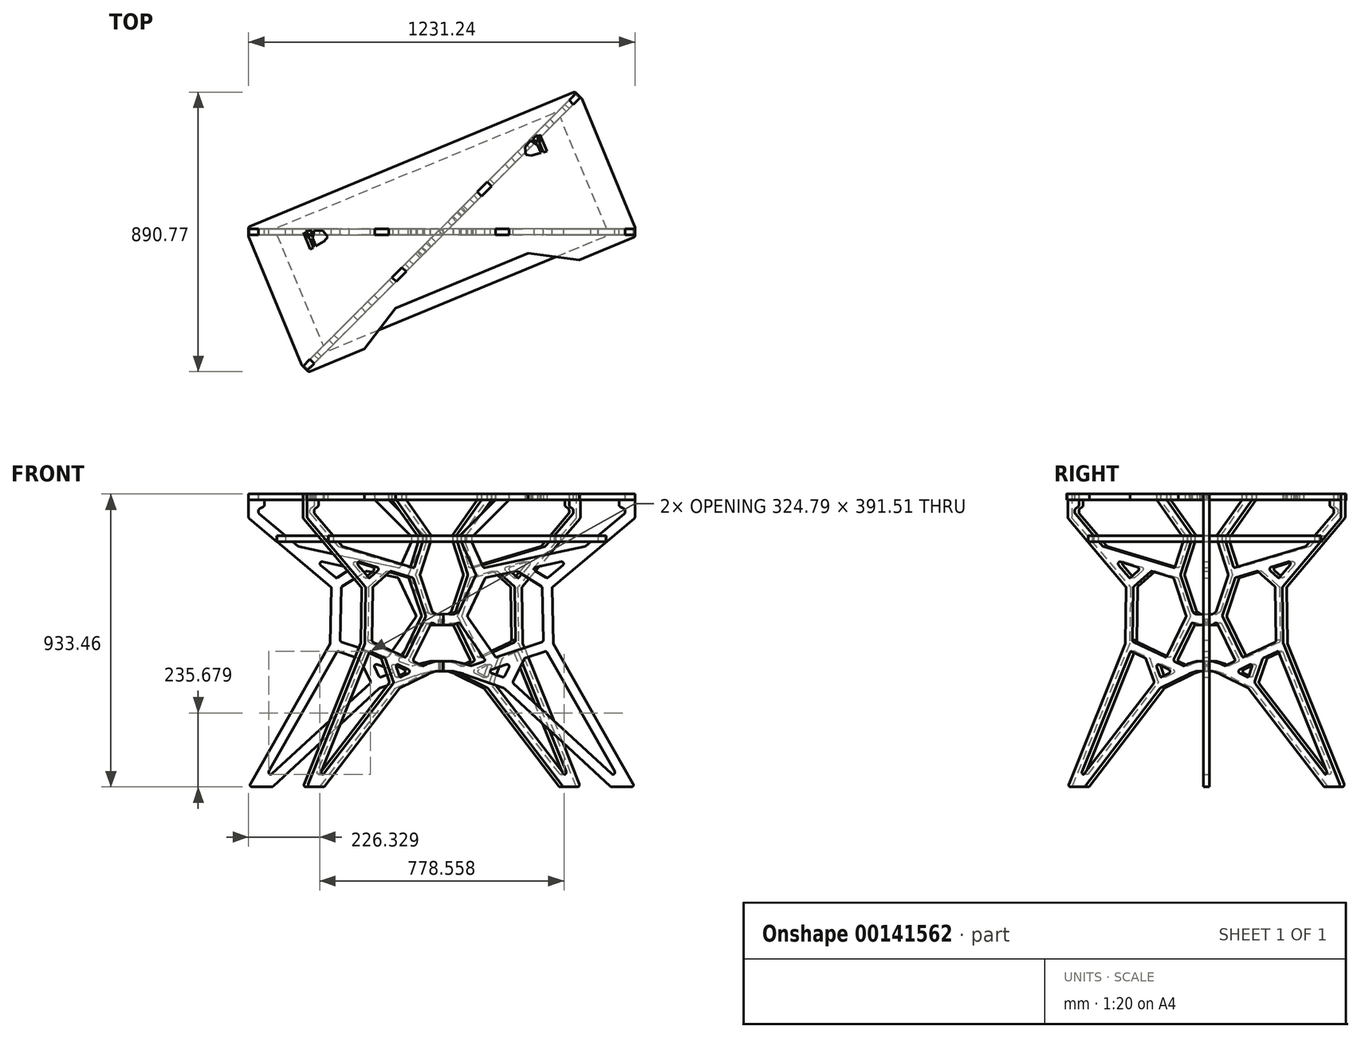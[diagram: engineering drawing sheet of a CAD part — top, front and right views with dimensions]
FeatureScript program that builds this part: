
annotation { "Feature Type Name" : "Feature", "Feature Type Description" : "" }
export const myFeature = defineFeature(function(context is Context, id is Id, definition is map)
    precondition{}
    {
        {
            var Q0;
            Q0=qCreatedBy(makeId("Front.planeOp"),FACE);
            var sketch = newSketch(context, id + "F0", { "sketchPlane" : qUnion([Q0])});
            skLineSegment(sketch, "E0.bottom", {"start": v(-726.46, -550.82) * mm, "end": v(-663.66, -550.82) * mm});
            skLineSegment(sketch, "E0.top", {"start": v(-737.38, 382.63) * mm, "end": v(-705.63, 382.63) * mm});
            skLineSegment(sketch, "E0.left", {"start": v(-737.38, -93.62) * mm, "end": v(-737.38, 230.23) * mm});
            skLineSegment(sketch, "E1", {"start": v(-705.63, 363.58) * mm, "end": v(-686.58, 363.58) * mm});
            skLineSegment(sketch, "E2.bottom", {"start": v(-737.38, 230.23) * mm, "end": v(493.44, 230.23) * mm, "construction": true});
            skLineSegment(sketch, "E2.top", {"start": v(-737.38, 211.18) * mm, "end": v(493.44, 211.18) * mm, "construction": true});
            skLineSegment(sketch, "E2.left", {"start": v(-737.38, 230.23) * mm, "end": v(-737.38, 211.18) * mm});
            skLineSegment(sketch, "E2.right", {"start": v(493.44, 230.23) * mm, "end": v(493.44, 211.18) * mm});
            skLineSegment(sketch, "E3", {"start": v(-735.1, 304.53) * mm, "end": v(-475.84, 87.44) * mm});
            skLineSegment(sketch, "E4", {"start": v(-473.57, 82.44) * mm, "end": v(-477.15, -92) * mm});
            skLineSegment(sketch, "E5", {"start": v(-477.98, -95.02) * mm, "end": v(-731.98, -541.32) * mm});
            skLineSegment(sketch, "E6", {"start": v(-737.38, -93.62) * mm, "end": v(493.78, -93.62) * mm, "construction": true});
            skLineSegment(sketch, "E7", {"start": v(-726.46, -550.82) * mm, "end": v(-661.18, -550.82) * mm});
            skLineSegment(sketch, "E8", {"start": v(-659.36, -549.13) * mm, "end": v(-321.3, -237.33) * mm});
            skLineSegment(sketch, "E9", {"start": v(-319.11, -236) * mm, "end": v(-190.82, -190.7) * mm});
            skLineSegment(sketch, "E10", {"start": v(-190.2, -190.52) * mm, "end": v(-123.3, -174.31) * mm});
            skLineSegment(sketch, "E11", {"start": v(-182.24, 230.23) * mm, "end": v(-228.58, 128.01) * mm});
            skLineSegment(sketch, "E12", {"start": v(-228.55, 122.7) * mm, "end": v(-175.03, 8.55) * mm});
            skLineSegment(sketch, "E13", {"start": v(-171.72, 5.38) * mm, "end": v(-124.24, -14.36) * mm});
            skLineSegment(sketch, "E14", {"start": v(-553, 193.46) * mm, "end": v(-261.6, 132.05) * mm, "construction": true});
            skLineSegment(sketch, "E15", {"start": v(-473.5, 85.48) * mm, "end": v(-383.92, 141.6) * mm, "construction": true});
            skLineSegment(sketch, "E16", {"start": v(-477.18, -93.62) * mm, "end": v(-239.21, -174.12) * mm, "construction": true});
            skLineSegment(sketch, "E17", {"start": v(-320.34, -236.44) * mm, "end": v(-364, -148.67) * mm, "construction": true});
            skLineSegment(sketch, "E18", {"start": v(-192.54, -20.35) * mm, "end": v(-278.62, -144.03) * mm, "construction": true});
            skLineSegment(sketch, "E19.0", {"start": v(-662.9, -509.21) * mm, "end": v(-350.73, -221.27) * mm});
            skLineSegment(sketch, "E20.0", {"start": v(-457.14, -122.59) * mm, "end": v(-672.73, -501.4) * mm});
            skLineSegment(sketch, "E21.0", {"start": v(-199.25, -160.05) * mm, "end": v(-123.3, -141.64) * mm});
            skLineSegment(sketch, "E21.1", {"start": v(-314.2, -200.6) * mm, "end": v(-280.77, -188.8) * mm});
            skLineSegment(sketch, "E22.0", {"start": v(-172.82, -28.55) * mm, "end": v(-124.24, -48.75) * mm});
            skLineSegment(sketch, "E22.1", {"start": v(-258.92, 112.68) * mm, "end": v(-204.28, -3.86) * mm});
            skLineSegment(sketch, "E23.0", {"start": v(-705.63, 324.22) * mm, "end": v(-705.63, 329.87) * mm});
            skLineSegment(sketch, "E24.0", {"start": v(-703.36, 319.36) * mm, "end": v(-580.12, 216.16) * mm});
            skLineSegment(sketch, "E25.0", {"start": v(-441.8, 83.23) * mm, "end": v(-445.22, -83.58) * mm});
            skLineSegment(sketch, "E26.0", {"start": v(-502.23, 166.54) * mm, "end": v(-421.69, 149.57) * mm});
            skLineSegment(sketch, "E27.0", {"start": v(-577.35, 214.82) * mm, "end": v(-259.88, 147.91) * mm});
            skLineSegment(sketch, "E28.0", {"start": v(-438.82, 88.48) * mm, "end": v(-363.71, 135.53) * mm});
            skLineSegment(sketch, "E29.0", {"start": v(-454.1, 116.37) * mm, "end": v(-419.62, 137.97) * mm});
            skLineSegment(sketch, "E30.0", {"start": v(-440.92, -89.12) * mm, "end": v(-298.8, -137.2) * mm});
            skLineSegment(sketch, "E31.0", {"start": v(-449.58, -119.71) * mm, "end": v(-387.8, -140.61) * mm});
            skLineSegment(sketch, "E32.0", {"start": v(-322, -197.44) * mm, "end": v(-335.83, -169.65) * mm});
            skLineSegment(sketch, "E33.0", {"start": v(-349.34, -213.78) * mm, "end": v(-384.15, -143.8) * mm});
            skLineSegment(sketch, "E34.0", {"start": v(-204.81, -10.18) * mm, "end": v(-291.55, -134.82) * mm});
            skLineSegment(sketch, "E35.0", {"start": v(-180.47, -30.78) * mm, "end": v(-258.14, -142.4) * mm});
            skLineSegment(sketch, "E36.trimOffspring", {"start": v(-507.62, 155.46) * mm, "end": v(-461.55, 116.88) * mm});
            skLineSegment(sketch, "E37.trimOffspring", {"start": v(-359.03, 136.36) * mm, "end": v(-263.36, 116.2) * mm});
            skLineSegment(sketch, "E38.trimOffspring", {"start": v(-254.96, -152.04) * mm, "end": v(-217.05, -164.86) * mm});
            skLineSegment(sketch, "E39.trimOffspring", {"start": v(-328.1, -160.8) * mm, "end": v(-280.85, -176.8) * mm});
            skLineSegment(sketch, "E40", {"start": v(-217.45, 230.23) * mm, "end": v(-182.24, 230.23) * mm});
            skPoint(sketch, "E41.orphan", {"position": v(-121.8, 363.58) * mm});
            skLineSegment(sketch, "E42.trimOffspring", {"start": v(-217.45, 230.23) * mm, "end": v(-252.78, 151.53) * mm});
            skPoint(sketch, "E43.visualSharp", {"position": v(-319.5, -202.47) * mm});
            skArc(sketch, "E43.filletArc", {"start": v(-322, -197.44) * mm, "mid": v(-318.7, -200.5) * mm, "end": v(-314.2, -200.6) * mm});
            skLineSegment(sketch, "E44.trimOffspring", {"start": v(-212.9, -164.83) * mm, "end": v(-199.87, -160.23) * mm});
            skPoint(sketch, "E45.visualSharp", {"position": v(-342.68, -155.88) * mm});
            skArc(sketch, "E45.filletArc", {"start": v(-328.1, -160.8) * mm, "mid": v(-334.93, -162.65) * mm, "end": v(-335.83, -169.65) * mm});
            skPoint(sketch, "E46.visualSharp", {"position": v(-263.45, -182.68) * mm});
            skArc(sketch, "E46.filletArc", {"start": v(-280.77, -188.8) * mm, "mid": v(-276.54, -182.77) * mm, "end": v(-280.85, -176.8) * mm});
            skPoint(sketch, "E47.visualSharp", {"position": v(-347.22, -218.04) * mm});
            skArc(sketch, "E47.filletArc", {"start": v(-350.73, -221.27) * mm, "mid": v(-348.79, -217.75) * mm, "end": v(-349.34, -213.78) * mm});
            skPoint(sketch, "E48.visualSharp", {"position": v(-385.31, -141.45) * mm});
            skArc(sketch, "E48.filletArc", {"start": v(-384.15, -143.8) * mm, "mid": v(-385.65, -141.85) * mm, "end": v(-387.8, -140.61) * mm});
            skPoint(sketch, "E49.visualSharp", {"position": v(-454.54, -118.03) * mm});
            skArc(sketch, "E49.filletArc", {"start": v(-449.58, -119.71) * mm, "mid": v(-453.88, -119.8) * mm, "end": v(-457.14, -122.59) * mm});
            skPoint(sketch, "E50.visualSharp", {"position": v(-692.94, -536.91) * mm});
            skArc(sketch, "E50.filletArc", {"start": v(-672.73, -501.4) * mm, "mid": v(-671.16, -509.51) * mm, "end": v(-662.9, -509.21) * mm});
            skPoint(sketch, "E51.visualSharp", {"position": v(-445.33, -87.63) * mm});
            skArc(sketch, "E51.filletArc", {"start": v(-445.23, -82.98) * mm, "mid": v(-444.08, -86.76) * mm, "end": v(-440.92, -89.12) * mm});
            skPoint(sketch, "E52.visualSharp", {"position": v(-294.28, -138.74) * mm});
            skArc(sketch, "E52.filletArc", {"start": v(-298.8, -137.2) * mm, "mid": v(-294.78, -137.22) * mm, "end": v(-291.55, -134.82) * mm});
            skPoint(sketch, "E53.visualSharp", {"position": v(-262.97, -149.33) * mm});
            skArc(sketch, "E53.filletArc", {"start": v(-258.14, -142.4) * mm, "mid": v(-258.96, -148) * mm, "end": v(-254.96, -152.04) * mm});
            skPoint(sketch, "E54.visualSharp", {"position": v(-214.97, -165.57) * mm});
            skArc(sketch, "E54.filletArc", {"start": v(-217.05, -164.86) * mm, "mid": v(-214.98, -165.2) * mm, "end": v(-212.9, -164.83) * mm});
            skPoint(sketch, "E55.visualSharp", {"position": v(-199.56, -160.12) * mm});
            skArc(sketch, "E55.filletArc", {"start": v(-199.25, -160.05) * mm, "mid": v(-199.56, -160.13) * mm, "end": v(-199.87, -160.23) * mm});
            skPoint(sketch, "E56.visualSharp", {"position": v(-190.51, -190.6) * mm});
            skArc(sketch, "E56.filletArc", {"start": v(-190.2, -190.52) * mm, "mid": v(-190.51, -190.6) * mm, "end": v(-190.82, -190.7) * mm});
            skPoint(sketch, "E57.visualSharp", {"position": v(-320.34, -236.44) * mm});
            skArc(sketch, "E57.filletArc", {"start": v(-319.11, -236) * mm, "mid": v(-320.27, -236.55) * mm, "end": v(-321.3, -237.33) * mm});
            skPoint(sketch, "E58.visualSharp", {"position": v(-177.54, -26.58) * mm});
            skArc(sketch, "E58.filletArc", {"start": v(-172.82, -28.55) * mm, "mid": v(-177.04, -28.32) * mm, "end": v(-180.47, -30.78) * mm});
            skPoint(sketch, "E59.visualSharp", {"position": v(-173.99, 6.32) * mm});
            skArc(sketch, "E59.filletArc", {"start": v(-175.03, 8.55) * mm, "mid": v(-173.67, 6.65) * mm, "end": v(-171.72, 5.38) * mm});
            skPoint(sketch, "E60.visualSharp", {"position": v(-202.72, -7.18) * mm});
            skArc(sketch, "E60.filletArc", {"start": v(-204.81, -10.18) * mm, "mid": v(-203.7, -7.1) * mm, "end": v(-204.28, -3.86) * mm});
            skPoint(sketch, "E61.visualSharp", {"position": v(-477.18, -93.62) * mm});
            skArc(sketch, "E61.filletArc", {"start": v(-477.98, -95.02) * mm, "mid": v(-477.37, -93.56) * mm, "end": v(-477.15, -92) * mm});
            skPoint(sketch, "E62.visualSharp", {"position": v(-473.5, 85.48) * mm});
            skArc(sketch, "E62.filletArc", {"start": v(-473.57, 82.44) * mm, "mid": v(-474.14, 85.2) * mm, "end": v(-475.84, 87.44) * mm});
            skPoint(sketch, "E63.visualSharp", {"position": v(-441.73, 86.66) * mm});
            skArc(sketch, "E63.filletArc", {"start": v(-438.82, 88.48) * mm, "mid": v(-440.97, 86.23) * mm, "end": v(-441.8, 83.23) * mm});
            skPoint(sketch, "E64.visualSharp", {"position": v(-458.02, 113.92) * mm});
            skArc(sketch, "E64.filletArc", {"start": v(-461.55, 116.88) * mm, "mid": v(-457.91, 115.42) * mm, "end": v(-454.1, 116.37) * mm});
            skPoint(sketch, "E65.visualSharp", {"position": v(-260.26, 115.55) * mm});
            skArc(sketch, "E65.filletArc", {"start": v(-258.92, 112.68) * mm, "mid": v(-260.72, 114.96) * mm, "end": v(-263.36, 116.2) * mm});
            skPoint(sketch, "E66.visualSharp", {"position": v(-361.54, 136.89) * mm});
            skArc(sketch, "E66.filletArc", {"start": v(-359.03, 136.36) * mm, "mid": v(-361.45, 136.4) * mm, "end": v(-363.71, 135.53) * mm});
            skPoint(sketch, "E67.visualSharp", {"position": v(-406.3, 146.32) * mm});
            skArc(sketch, "E67.filletArc", {"start": v(-419.62, 137.97) * mm, "mid": v(-416.74, 144.46) * mm, "end": v(-421.69, 149.57) * mm});
            skPoint(sketch, "E68.visualSharp", {"position": v(-254.88, 146.86) * mm});
            skArc(sketch, "E68.filletArc", {"start": v(-259.88, 147.91) * mm, "mid": v(-255.7, 148.47) * mm, "end": v(-252.78, 151.53) * mm});
            skPoint(sketch, "E69.visualSharp", {"position": v(-229.79, 125.35) * mm});
            skArc(sketch, "E69.filletArc", {"start": v(-228.58, 128.01) * mm, "mid": v(-229.15, 125.35) * mm, "end": v(-228.55, 122.7) * mm});
            skPoint(sketch, "E70.visualSharp", {"position": v(-527.12, 171.78) * mm});
            skArc(sketch, "E70.filletArc", {"start": v(-502.23, 166.54) * mm, "mid": v(-509.25, 163.1) * mm, "end": v(-507.62, 155.46) * mm});
            skPoint(sketch, "E71.visualSharp", {"position": v(-578.9, 215.14) * mm});
            skArc(sketch, "E71.filletArc", {"start": v(-580.12, 216.16) * mm, "mid": v(-578.82, 215.32) * mm, "end": v(-577.35, 214.82) * mm});
            skLineSegment(sketch, "E72", {"start": v(-737.38, 382.63) * mm, "end": v(-737.38, 309.4) * mm});
            skPoint(sketch, "E73.visualSharp", {"position": v(-737.38, 306.43) * mm});
            skArc(sketch, "E73.filletArc", {"start": v(-737.38, 309.4) * mm, "mid": v(-736.78, 306.71) * mm, "end": v(-735.1, 304.53) * mm});
            skPoint(sketch, "E74.visualSharp", {"position": v(-705.63, 321.26) * mm});
            skArc(sketch, "E74.filletArc", {"start": v(-705.63, 324.22) * mm, "mid": v(-705.03, 321.54) * mm, "end": v(-703.36, 319.36) * mm});
            skArc(sketch, "E75.MirrorCS", {"start": v(234.38, -95.02) * mm, "mid": v(233.78, -93.56) * mm, "end": v(233.55, -92) * mm});
            skArc(sketch, "E76.MirrorCS", {"start": v(195.22, 88.48) * mm, "mid": v(197.38, 86.23) * mm, "end": v(198.2, 83.23) * mm});
            skArc(sketch, "E77.MirrorCS", {"start": v(-26.54, -164.86) * mm, "mid": v(-28.62, -165.2) * mm, "end": v(-30.7, -164.83) * mm});
            skArc(sketch, "E78.MirrorCS", {"start": v(-44.35, -160.05) * mm, "mid": v(-44.04, -160.13) * mm, "end": v(-43.73, -160.23) * mm});
            skLineSegment(sketch, "E79.MirrorCS", {"start": v(-30.7, -164.83) * mm, "end": v(-43.73, -160.23) * mm});
            skArc(sketch, "E80.MirrorCS", {"start": v(229.97, 82.44) * mm, "mid": v(230.54, 85.2) * mm, "end": v(232.25, 87.44) * mm});
            skArc(sketch, "E81.MirrorCS", {"start": v(75.51, -236) * mm, "mid": v(76.68, -236.55) * mm, "end": v(77.7, -237.33) * mm});
            skLineSegment(sketch, "E82.MirrorCS", {"start": v(78.41, -197.44) * mm, "end": v(92.23, -169.65) * mm});
            skArc(sketch, "E83.MirrorCS", {"start": v(-70.78, -28.55) * mm, "mid": v(-66.56, -28.32) * mm, "end": v(-63.13, -30.78) * mm});
            skArc(sketch, "E84.MirrorCS", {"start": v(-53.4, -190.52) * mm, "mid": v(-53.08, -190.6) * mm, "end": v(-52.78, -190.7) * mm});
            skArc(sketch, "E85.MirrorCS", {"start": v(115.43, 136.36) * mm, "mid": v(117.86, 136.4) * mm, "end": v(120.11, 135.53) * mm});
            skArc(sketch, "E86.MirrorCS", {"start": v(78.41, -197.44) * mm, "mid": v(75.1, -200.5) * mm, "end": v(70.61, -200.6) * mm});
            skArc(sketch, "E87.MirrorCS", {"start": v(84.51, -160.8) * mm, "mid": v(91.33, -162.65) * mm, "end": v(92.23, -169.65) * mm});
            skArc(sketch, "E88.MirrorCS", {"start": v(336.52, 216.16) * mm, "mid": v(335.22, 215.32) * mm, "end": v(333.75, 214.82) * mm});
            skArc(sketch, "E89.MirrorCS", {"start": v(15.32, 112.68) * mm, "mid": v(17.13, 114.96) * mm, "end": v(19.76, 116.2) * mm});
            skArc(sketch, "E90.MirrorCS", {"start": v(462.03, 324.22) * mm, "mid": v(461.44, 321.54) * mm, "end": v(459.76, 319.36) * mm});
            skArc(sketch, "E91.MirrorCS", {"start": v(217.96, 116.88) * mm, "mid": v(214.32, 115.42) * mm, "end": v(210.5, 116.37) * mm});
            skArc(sketch, "E92.MirrorCS", {"start": v(140.55, -143.8) * mm, "mid": v(142.06, -141.85) * mm, "end": v(144.2, -140.61) * mm});
            skArc(sketch, "E93.MirrorCS", {"start": v(16.29, 147.91) * mm, "mid": v(12.1, 148.47) * mm, "end": v(9.19, 151.53) * mm});
            skArc(sketch, "E94.MirrorCS", {"start": v(-68.57, 8.55) * mm, "mid": v(-69.93, 6.65) * mm, "end": v(-71.88, 5.38) * mm});
            skArc(sketch, "E95.MirrorCS", {"start": v(107.13, -221.27) * mm, "mid": v(105.19, -217.75) * mm, "end": v(105.75, -213.78) * mm});
            skArc(sketch, "E96.MirrorCS", {"start": v(55.2, -137.2) * mm, "mid": v(51.18, -137.22) * mm, "end": v(47.95, -134.82) * mm});
            skLineSegment(sketch, "E97.MirrorCS", {"start": v(210.5, 116.37) * mm, "end": v(176.03, 137.97) * mm});
            skLineSegment(sketch, "E98.MirrorCS", {"start": v(76.75, -236.44) * mm, "end": v(120.4, -148.67) * mm, "construction": true});
            skArc(sketch, "E99.MirrorCS", {"start": v(-15.02, 128.01) * mm, "mid": v(-14.45, 125.35) * mm, "end": v(-15.05, 122.7) * mm});
            skArc(sketch, "E100.MirrorCS", {"start": v(176.03, 137.97) * mm, "mid": v(173.15, 144.46) * mm, "end": v(178.09, 149.57) * mm});
            skArc(sketch, "E101.MirrorCS", {"start": v(201.64, -82.98) * mm, "mid": v(200.49, -86.76) * mm, "end": v(197.32, -89.12) * mm});
            skArc(sketch, "E102.MirrorCS", {"start": v(205.99, -119.71) * mm, "mid": v(210.28, -119.8) * mm, "end": v(213.54, -122.59) * mm});
            skArc(sketch, "E103.MirrorCS", {"start": v(493.78, 309.4) * mm, "mid": v(493.19, 306.71) * mm, "end": v(491.5, 304.53) * mm});
            skArc(sketch, "E104.MirrorCS", {"start": v(258.64, 166.54) * mm, "mid": v(265.66, 163.1) * mm, "end": v(264.02, 155.46) * mm});
            skLineSegment(sketch, "E105.MirrorCS", {"start": v(11.37, -152.04) * mm, "end": v(-26.54, -164.86) * mm});
            skLineSegment(sketch, "E106.MirrorCS", {"start": v(493.78, -550.82) * mm, "end": v(417.58, -550.82) * mm});
            skLineSegment(sketch, "E107.MirrorCS", {"start": v(70.61, -200.6) * mm, "end": v(37.18, -188.8) * mm});
            skLineSegment(sketch, "E108.MirrorCS", {"start": v(493.78, 230.23) * mm, "end": v(493.78, 211.18) * mm});
            skArc(sketch, "E109.MirrorCS", {"start": v(429.13, -501.4) * mm, "mid": v(427.56, -509.51) * mm, "end": v(419.3, -509.21) * mm});
            skLineSegment(sketch, "E110.MirrorCS", {"start": v(84.51, -160.8) * mm, "end": v(37.26, -176.8) * mm});
            skArc(sketch, "E111.MirrorCS", {"start": v(37.18, -188.8) * mm, "mid": v(32.94, -182.77) * mm, "end": v(37.26, -176.8) * mm});
            skArc(sketch, "E112.MirrorCS", {"start": v(14.54, -142.4) * mm, "mid": v(15.36, -148) * mm, "end": v(11.37, -152.04) * mm});
            skArc(sketch, "E113.MirrorCS", {"start": v(-38.78, -10.18) * mm, "mid": v(-39.9, -7.1) * mm, "end": v(-39.32, -3.86) * mm});
            skLineSegment(sketch, "E114.MirrorCS", {"start": v(229.91, 85.48) * mm, "end": v(140.32, 141.6) * mm, "construction": true});
            skLineSegment(sketch, "E115.MirrorCS", {"start": v(105.75, -213.78) * mm, "end": v(140.55, -143.8) * mm});
            skLineSegment(sketch, "E116.MirrorCS", {"start": v(-26.15, 230.23) * mm, "end": v(-61.35, 230.23) * mm});
            skLineSegment(sketch, "E117.MirrorCS", {"start": v(264.02, 155.46) * mm, "end": v(217.96, 116.88) * mm});
            skLineSegment(sketch, "E118.MirrorCS", {"start": v(462.03, 324.22) * mm, "end": v(462.03, 329.87) * mm});
            skLineSegment(sketch, "E119.MirrorCS", {"start": v(-737.04, 230.23) * mm, "end": v(-737.04, 211.18) * mm});
            skLineSegment(sketch, "E120.MirrorCS", {"start": v(482.86, -550.82) * mm, "end": v(420.06, -550.82) * mm});
            skLineSegment(sketch, "E121.MirrorCS", {"start": v(-71.88, 5.38) * mm, "end": v(-119.36, -14.36) * mm});
            skPoint(sketch, "E122.MirrorP", {"position": v(-28.62, -165.57) * mm});
            skLineSegment(sketch, "E123.MirrorCS", {"start": v(-38.78, -10.18) * mm, "end": v(47.95, -134.82) * mm});
            skLineSegment(sketch, "E124.MirrorCS", {"start": v(-51.05, -20.35) * mm, "end": v(35.03, -144.03) * mm, "construction": true});
            skLineSegment(sketch, "E125.MirrorCS", {"start": v(309.41, 193.46) * mm, "end": v(18.01, 132.05) * mm, "construction": true});
            skLineSegment(sketch, "E126.MirrorCS", {"start": v(233.58, -93.62) * mm, "end": v(-4.38, -174.12) * mm, "construction": true});
            skLineSegment(sketch, "E127.MirrorCS", {"start": v(258.64, 166.54) * mm, "end": v(178.09, 149.57) * mm});
            skPoint(sketch, "E128.MirrorP", {"position": v(99.08, -155.88) * mm});
            skLineSegment(sketch, "E129.MirrorCS", {"start": v(-70.78, -28.55) * mm, "end": v(-119.36, -48.75) * mm});
            skPoint(sketch, "E130.MirrorP", {"position": v(-66.05, -26.58) * mm});
            skPoint(sketch, "E131.MirrorP", {"position": v(162.7, 146.32) * mm});
            skPoint(sketch, "E132.MirrorP", {"position": v(198.13, 86.66) * mm});
            skLineSegment(sketch, "E133.MirrorCS", {"start": v(-63.13, -30.78) * mm, "end": v(14.54, -142.4) * mm});
            skLineSegment(sketch, "E134.MirrorCS", {"start": v(205.99, -119.71) * mm, "end": v(144.2, -140.61) * mm});
            skLineSegment(sketch, "E135.MirrorCS", {"start": v(195.22, 88.48) * mm, "end": v(120.11, 135.53) * mm});
            skPoint(sketch, "E136.MirrorP", {"position": v(50.68, -138.74) * mm});
            skLineSegment(sketch, "E137.MirrorCS", {"start": v(-44.35, -160.05) * mm, "end": v(-120.3, -141.64) * mm});
            skLineSegment(sketch, "E138.MirrorCS", {"start": v(-53.4, -190.52) * mm, "end": v(-120.3, -174.31) * mm});
            skLineSegment(sketch, "E139.MirrorCS", {"start": v(197.32, -89.12) * mm, "end": v(55.2, -137.2) * mm});
            skPoint(sketch, "E140.MirrorP", {"position": v(462.03, 321.26) * mm});
            skPoint(sketch, "E141.MirrorP", {"position": v(16.66, 115.55) * mm});
            skPoint(sketch, "E142.MirrorP", {"position": v(-40.87, -7.18) * mm});
            skPoint(sketch, "E143.MirrorP", {"position": v(11.28, 146.86) * mm});
            skLineSegment(sketch, "E144.MirrorCS", {"start": v(-26.15, 230.23) * mm, "end": v(9.19, 151.53) * mm});
            skLineSegment(sketch, "E145.MirrorCS", {"start": v(419.3, -509.21) * mm, "end": v(107.13, -221.27) * mm});
            skLineSegment(sketch, "E146.MirrorCS", {"start": v(-15.05, 122.7) * mm, "end": v(-68.57, 8.55) * mm});
            skLineSegment(sketch, "E147.MirrorCS", {"start": v(198.2, 83.23) * mm, "end": v(201.62, -83.58) * mm});
            skLineSegment(sketch, "E148.MirrorCS", {"start": v(459.76, 319.36) * mm, "end": v(336.52, 216.16) * mm});
            skLineSegment(sketch, "E149.MirrorCS", {"start": v(493.78, 382.63) * mm, "end": v(493.78, 309.4) * mm});
            skPoint(sketch, "E150.MirrorP", {"position": v(19.86, -182.68) * mm});
            skPoint(sketch, "E151.MirrorP", {"position": v(214.42, 113.92) * mm});
            skLineSegment(sketch, "E152.MirrorCS", {"start": v(-61.35, 230.23) * mm, "end": v(-15.02, 128.01) * mm});
            skPoint(sketch, "E153.MirrorP", {"position": v(283.52, 171.78) * mm});
            skPoint(sketch, "E154.MirrorP", {"position": v(141.72, -141.45) * mm});
            skPoint(sketch, "E155.MirrorP", {"position": v(493.78, 306.43) * mm});
            skPoint(sketch, "E156.MirrorP", {"position": v(229.91, 85.48) * mm});
            skLineSegment(sketch, "E157.MirrorCS", {"start": v(213.54, -122.59) * mm, "end": v(429.13, -501.4) * mm});
            skLineSegment(sketch, "E158.MirrorCS", {"start": v(493.78, -93.62) * mm, "end": v(493.78, 230.23) * mm});
            skPoint(sketch, "E159.MirrorP", {"position": v(19.37, -149.33) * mm});
            skLineSegment(sketch, "E160.MirrorCS", {"start": v(333.75, 214.82) * mm, "end": v(16.29, 147.91) * mm});
            skPoint(sketch, "E161.MirrorP", {"position": v(335.3, 215.14) * mm});
            skLineSegment(sketch, "E162.MirrorCS", {"start": v(491.5, 304.53) * mm, "end": v(232.25, 87.44) * mm});
            skPoint(sketch, "E163.MirrorP", {"position": v(75.9, -202.47) * mm});
            skPoint(sketch, "E164.MirrorP", {"position": v(-53.08, -190.6) * mm});
            skLineSegment(sketch, "E165.MirrorCS", {"start": v(75.51, -236) * mm, "end": v(-52.78, -190.7) * mm});
            skPoint(sketch, "E166.MirrorP", {"position": v(117.94, 136.89) * mm});
            skPoint(sketch, "E167.MirrorP", {"position": v(-13.8, 125.35) * mm});
            skLineSegment(sketch, "E168.MirrorCS", {"start": v(415.76, -549.13) * mm, "end": v(77.7, -237.33) * mm});
            skLineSegment(sketch, "E169.MirrorCS", {"start": v(234.38, -95.02) * mm, "end": v(488.38, -541.32) * mm});
            skPoint(sketch, "E170.MirrorP", {"position": v(210.95, -118.03) * mm});
            skLineSegment(sketch, "E171.MirrorCS", {"start": v(15.32, 112.68) * mm, "end": v(-39.32, -3.86) * mm});
            skPoint(sketch, "E172.MirrorP", {"position": v(-69.61, 6.32) * mm});
            skPoint(sketch, "E173.MirrorP", {"position": v(-44.04, -160.12) * mm});
            skPoint(sketch, "E174.MirrorP", {"position": v(76.75, -236.44) * mm});
            skPoint(sketch, "E175.MirrorP", {"position": v(103.63, -218.04) * mm});
            skPoint(sketch, "E176.MirrorP", {"position": v(201.73, -87.63) * mm});
            skLineSegment(sketch, "E177.MirrorCS", {"start": v(229.97, 82.44) * mm, "end": v(233.55, -92) * mm});
            skLineSegment(sketch, "E178.MirrorCS", {"start": v(115.43, 136.36) * mm, "end": v(19.76, 116.2) * mm});
            skPoint(sketch, "E179.MirrorP", {"position": v(233.58, -93.62) * mm});
            skLineSegment(sketch, "E180", {"start": v(-686.58, 363.58) * mm, "end": v(-686.58, 348.2) * mm});
            skLineSegment(sketch, "E181", {"start": v(-689.75, 342.7) * mm, "end": v(-702.45, 335.37) * mm});
            skLineSegment(sketch, "E182.trimOffspring", {"start": v(-705.63, 363.58) * mm, "end": v(-705.63, 382.63) * mm});
            skPoint(sketch, "E183.visualSharp", {"position": v(-705.63, 333.54) * mm});
            skArc(sketch, "E183.filletArc", {"start": v(-702.45, 335.37) * mm, "mid": v(-704.78, 333.04) * mm, "end": v(-705.63, 329.87) * mm});
            skPoint(sketch, "E184.visualSharp", {"position": v(-686.58, 344.53) * mm});
            skArc(sketch, "E184.filletArc", {"start": v(-689.75, 342.7) * mm, "mid": v(-687.43, 345.03) * mm, "end": v(-686.58, 348.2) * mm});
            skLineSegment(sketch, "E185.trimOffspring", {"start": v(462.03, 382.63) * mm, "end": v(493.78, 382.63) * mm});
            skLineSegment(sketch, "E186", {"start": v(-182.24, 230.23) * mm, "end": v(-182.24, 249.28) * mm});
            skLineSegment(sketch, "E187", {"start": v(-182.24, 249.28) * mm, "end": v(-217.45, 249.28) * mm});
            skLineSegment(sketch, "E188", {"start": v(-217.45, 249.28) * mm, "end": v(-217.45, 230.23) * mm});
            skLineSegment(sketch, "E189", {"start": v(-61.35, 230.23) * mm, "end": v(-61.35, 249.28) * mm});
            skLineSegment(sketch, "E190", {"start": v(-61.35, 249.28) * mm, "end": v(-26.15, 249.28) * mm});
            skLineSegment(sketch, "E191", {"start": v(-26.15, 249.28) * mm, "end": v(-26.15, 230.23) * mm});
            skLineSegment(sketch, "E192", {"start": v(462.03, 363.58) * mm, "end": v(442.98, 363.58) * mm});
            skLineSegment(sketch, "E193", {"start": v(442.98, 363.58) * mm, "end": v(442.98, 348.2) * mm});
            skLineSegment(sketch, "E194", {"start": v(446.16, 342.7) * mm, "end": v(458.86, 335.37) * mm});
            skLineSegment(sketch, "E195.trimOffspring", {"start": v(462.03, 363.58) * mm, "end": v(462.03, 382.63) * mm});
            skPoint(sketch, "E196.visualSharp", {"position": v(442.98, 344.53) * mm});
            skArc(sketch, "E196.filletArc", {"start": v(442.98, 348.2) * mm, "mid": v(443.83, 345.03) * mm, "end": v(446.16, 342.7) * mm});
            skPoint(sketch, "E197.visualSharp", {"position": v(462.03, 333.54) * mm});
            skArc(sketch, "E197.filletArc", {"start": v(462.03, 329.87) * mm, "mid": v(461.18, 333.04) * mm, "end": v(458.86, 335.37) * mm});
            skPoint(sketch, "E198.visualSharp", {"position": v(417.58, -550.82) * mm});
            skArc(sketch, "E198.filletArc", {"start": v(415.76, -549.13) * mm, "mid": v(417.75, -550.38) * mm, "end": v(420.06, -550.82) * mm});
            skPoint(sketch, "E199.visualSharp", {"position": v(493.78, -550.82) * mm});
            skArc(sketch, "E199.filletArc", {"start": v(482.86, -550.82) * mm, "mid": v(488.35, -547.66) * mm, "end": v(488.38, -541.32) * mm});
            skPoint(sketch, "E200.visualSharp", {"position": v(-737.38, -550.82) * mm});
            skArc(sketch, "E200.filletArc", {"start": v(-731.98, -541.32) * mm, "mid": v(-731.95, -547.66) * mm, "end": v(-726.46, -550.82) * mm});
            skPoint(sketch, "E201.visualSharp", {"position": v(-661.18, -550.82) * mm});
            skArc(sketch, "E201.filletArc", {"start": v(-663.66, -550.82) * mm, "mid": v(-661.35, -550.38) * mm, "end": v(-659.36, -549.13) * mm});
            skPoint(sketch, "E202.visualSharp", {"position": v(-121.8, -173.95) * mm});
            skArc(sketch, "E202.filletArc", {"start": v(-120.3, -174.31) * mm, "mid": v(-121.8, -174.13) * mm, "end": v(-123.3, -174.31) * mm});
            skPoint(sketch, "E203.visualSharp", {"position": v(-121.8, -141.28) * mm});
            skArc(sketch, "E203.filletArc", {"start": v(-120.3, -141.64) * mm, "mid": v(-121.8, -141.47) * mm, "end": v(-123.3, -141.64) * mm});
            skPoint(sketch, "E204.visualSharp", {"position": v(-121.8, -49.76) * mm});
            skArc(sketch, "E204.filletArc", {"start": v(-124.24, -48.75) * mm, "mid": v(-121.8, -49.23) * mm, "end": v(-119.36, -48.75) * mm});
            skPoint(sketch, "E205.visualSharp", {"position": v(-121.8, -15.38) * mm});
            skArc(sketch, "E205.filletArc", {"start": v(-124.24, -14.36) * mm, "mid": v(-121.8, -14.85) * mm, "end": v(-119.36, -14.36) * mm});
            skLineSegment(sketch, "E206", {"start": v(-121.8, -14.85) * mm, "end": v(-121.8, -49.23) * mm});
            skPoint(sketch, "E207", {"position": v(-121.8, -32.04) * mm});
            skLineSegment(sketch, "E208", {"start": v(-121.8, -32.04) * mm, "end": v(-79.18, -32.04) * mm});
            skLineSegment(sketch, "E209", {"start": v(-121.8, -32.04) * mm, "end": v(-164.42, -32.04) * mm});
            skLineSegment(sketch, "E210", {"start": v(-121.8, -141.47) * mm, "end": v(-121.8, -174.13) * mm});
            skPoint(sketch, "E211", {"position": v(-121.8, -157.8) * mm});
            skLineSegment(sketch, "E212", {"start": v(-121.8, -157.8) * mm, "end": v(-53.62, -157.8) * mm});
            skLineSegment(sketch, "E213", {"start": v(-121.8, -157.8) * mm, "end": v(-189.97, -157.8) * mm});
            skSolve(sketch);
        }
        {
            var Q0;
            Q0=qCreatedBy(makeId("Top.planeOp"),FACE);
            cPlane(context, id + "F1", {"entities" : qUnion([Q0]), "cplaneType" : CPlaneType.OFFSET, "offset" : 230.23 * mm, "width" : 152.4 * mm, "height" : 152.4 * mm});
        }
        {
            var Q0;
            Q0=qCreatedBy(id+"F1.planeOp",FACE);
            cPlane(context, id + "F2", {"entities" : qUnion([Q0]), "cplaneType" : CPlaneType.OFFSET, "offset" : 133.35 * mm, "width" : 152.4 * mm, "height" : 152.4 * mm});
        }
        {
            var Q0;
            Q0=sQuery(id+"F0.wireOp",EDGE,"E206");
            cPlane(context, id + "F3", {"entities" : qUnion([Q0]), "cplaneType" : CPlaneType.LINE_ANGLE, "offset" : 25.4 * mm, "angle" : 45 * degree, "width" : 152.4 * mm, "height" : 152.4 * mm});
        }
        {
            var Q0;
            Q0=qCreatedBy(id+"F3.planeOp",FACE);
            var sketch = newSketch(context, id + "F4", { "sketchPlane" : qUnion([Q0])});
            skLineSegment(sketch, "E214.bottom", {"start": v(-518.53, -550.77) * mm, "end": v(-455.73, -550.77) * mm});
            skLineSegment(sketch, "E214.top", {"start": v(-529.45, 382.68) * mm, "end": v(-497.7, 382.68) * mm});
            skLineSegment(sketch, "E215", {"start": v(-497.7, 363.63) * mm, "end": v(-478.65, 363.63) * mm});
            skLineSegment(sketch, "E216", {"start": v(-527.18, 304.58) * mm, "end": v(-267.92, 87.48) * mm});
            skLineSegment(sketch, "E217", {"start": v(-265.64, 82.49) * mm, "end": v(-269.22, -91.96) * mm});
            skLineSegment(sketch, "E218", {"start": v(-270.05, -94.97) * mm, "end": v(-524.05, -541.28) * mm});
            skLineSegment(sketch, "E219", {"start": v(-518.53, -550.77) * mm, "end": v(-453.25, -550.77) * mm});
            skLineSegment(sketch, "E220", {"start": v(-451.43, -549.09) * mm, "end": v(-113.38, -237.28) * mm});
            skLineSegment(sketch, "E221", {"start": v(-111.18, -235.96) * mm, "end": v(17.1, -190.66) * mm});
            skLineSegment(sketch, "E222", {"start": v(17.73, -190.48) * mm, "end": v(49.67, -182.74) * mm});
            skLineSegment(sketch, "E223", {"start": v(25.68, 230.28) * mm, "end": v(-20.65, 128.06) * mm});
            skLineSegment(sketch, "E224", {"start": v(-20.62, 122.74) * mm, "end": v(32.9, 8.6) * mm});
            skLineSegment(sketch, "E225", {"start": v(36.21, 5.43) * mm, "end": v(49.67, -0.17) * mm});
            skLineSegment(sketch, "E226.0", {"start": v(-454.97, -509.17) * mm, "end": v(-142.8, -221.23) * mm});
            skLineSegment(sketch, "E227.0", {"start": v(-249.2, -122.54) * mm, "end": v(-464.8, -501.36) * mm});
            skLineSegment(sketch, "E228.0", {"start": v(8.68, -160) * mm, "end": v(49.67, -150.07) * mm});
            skLineSegment(sketch, "E228.1", {"start": v(-106.28, -200.56) * mm, "end": v(-72.85, -188.75) * mm});
            skLineSegment(sketch, "E229.1", {"start": v(-50.99, 112.73) * mm, "end": v(3.65, -3.82) * mm});
            skLineSegment(sketch, "E230.0", {"start": v(-497.7, 324.27) * mm, "end": v(-497.7, 329.92) * mm});
            skLineSegment(sketch, "E231.0", {"start": v(-495.43, 319.4) * mm, "end": v(-411.75, 249.33) * mm});
            skLineSegment(sketch, "E232.0", {"start": v(-233.87, 83.27) * mm, "end": v(-237.3, -83.53) * mm});
            skLineSegment(sketch, "E233.0", {"start": v(-294.3, 166.59) * mm, "end": v(-213.76, 149.61) * mm});
            skLineSegment(sketch, "E234.0", {"start": v(-369.42, 214.86) * mm, "end": v(-51.96, 147.96) * mm});
            skLineSegment(sketch, "E235.0", {"start": v(-230.9, 88.53) * mm, "end": v(-155.78, 135.57) * mm});
            skLineSegment(sketch, "E236.0", {"start": v(-246.18, 116.42) * mm, "end": v(-211.7, 138.02) * mm});
            skLineSegment(sketch, "E237.0", {"start": v(-233, -89.08) * mm, "end": v(-90.87, -137.16) * mm});
            skLineSegment(sketch, "E238.0", {"start": v(-241.65, -119.67) * mm, "end": v(-179.87, -140.57) * mm});
            skLineSegment(sketch, "E239.0", {"start": v(-114.08, -197.4) * mm, "end": v(-127.9, -169.6) * mm});
            skLineSegment(sketch, "E240.0", {"start": v(-141.42, -213.73) * mm, "end": v(-176.22, -143.76) * mm});
            skLineSegment(sketch, "E241.0", {"start": v(3.11, -10.14) * mm, "end": v(-83.62, -134.77) * mm});
            skLineSegment(sketch, "E242.0", {"start": v(27.46, -30.74) * mm, "end": v(-50.21, -142.35) * mm});
            skLineSegment(sketch, "E243.trimOffspring", {"start": v(-299.7, 155.5) * mm, "end": v(-253.63, 116.93) * mm});
            skLineSegment(sketch, "E244.trimOffspring", {"start": v(-151.1, 136.4) * mm, "end": v(-55.43, 116.24) * mm});
            skLineSegment(sketch, "E245.trimOffspring", {"start": v(-47.04, -152) * mm, "end": v(-9.13, -164.82) * mm});
            skLineSegment(sketch, "E246.trimOffspring", {"start": v(-120.18, -160.76) * mm, "end": v(-72.93, -176.75) * mm});
            skLineSegment(sketch, "E247", {"start": v(8.08, 230.28) * mm, "end": v(25.68, 230.28) * mm});
            skPoint(sketch, "E248.orphan", {"position": v(86.13, 363.63) * mm});
            skLineSegment(sketch, "E249.trimOffspring", {"start": v(-9.52, 230.28) * mm, "end": v(-44.85, 151.57) * mm});
            skPoint(sketch, "E250.visualSharp", {"position": v(-111.58, -202.43) * mm});
            skArc(sketch, "E250.filletArc", {"start": v(-114.08, -197.4) * mm, "mid": v(-110.78, -200.46) * mm, "end": v(-106.28, -200.56) * mm});
            skLineSegment(sketch, "E251.trimOffspring", {"start": v(-4.98, -164.79) * mm, "end": v(8.06, -160.19) * mm});
            skPoint(sketch, "E252.visualSharp", {"position": v(-134.75, -155.83) * mm});
            skArc(sketch, "E252.filletArc", {"start": v(-120.18, -160.76) * mm, "mid": v(-127, -162.6) * mm, "end": v(-127.9, -169.6) * mm});
            skPoint(sketch, "E253.visualSharp", {"position": v(-55.52, -182.64) * mm});
            skArc(sketch, "E253.filletArc", {"start": v(-72.85, -188.75) * mm, "mid": v(-68.61, -182.72) * mm, "end": v(-72.93, -176.75) * mm});
            skPoint(sketch, "E254.visualSharp", {"position": v(-139.3, -218) * mm});
            skArc(sketch, "E254.filletArc", {"start": v(-142.8, -221.23) * mm, "mid": v(-140.86, -217.7) * mm, "end": v(-141.42, -213.73) * mm});
            skPoint(sketch, "E255.visualSharp", {"position": v(-177.39, -141.4) * mm});
            skArc(sketch, "E255.filletArc", {"start": v(-176.22, -143.76) * mm, "mid": v(-177.73, -141.8) * mm, "end": v(-179.87, -140.57) * mm});
            skPoint(sketch, "E256.visualSharp", {"position": v(-246.62, -117.99) * mm});
            skArc(sketch, "E256.filletArc", {"start": v(-241.65, -119.67) * mm, "mid": v(-245.95, -119.75) * mm, "end": v(-249.2, -122.54) * mm});
            skPoint(sketch, "E257.visualSharp", {"position": v(-485, -536.87) * mm});
            skArc(sketch, "E257.filletArc", {"start": v(-464.8, -501.36) * mm, "mid": v(-463.23, -509.47) * mm, "end": v(-454.97, -509.17) * mm});
            skPoint(sketch, "E258.visualSharp", {"position": v(-237.4, -87.59) * mm});
            skArc(sketch, "E258.filletArc", {"start": v(-237.3, -82.93) * mm, "mid": v(-236.16, -86.71) * mm, "end": v(-233, -89.08) * mm});
            skPoint(sketch, "E259.visualSharp", {"position": v(-86.35, -138.7) * mm});
            skArc(sketch, "E259.filletArc", {"start": v(-90.87, -137.16) * mm, "mid": v(-86.85, -137.18) * mm, "end": v(-83.62, -134.77) * mm});
            skPoint(sketch, "E260.visualSharp", {"position": v(-55.04, -149.28) * mm});
            skArc(sketch, "E260.filletArc", {"start": v(-50.21, -142.35) * mm, "mid": v(-51.03, -147.96) * mm, "end": v(-47.04, -152) * mm});
            skPoint(sketch, "E261.visualSharp", {"position": v(-7.05, -165.52) * mm});
            skArc(sketch, "E261.filletArc", {"start": v(-9.13, -164.82) * mm, "mid": v(-7.05, -165.15) * mm, "end": v(-4.98, -164.79) * mm});
            skPoint(sketch, "E262.visualSharp", {"position": v(8.37, -160.08) * mm});
            skArc(sketch, "E262.filletArc", {"start": v(8.68, -160) * mm, "mid": v(8.37, -160.09) * mm, "end": v(8.06, -160.19) * mm});
            skPoint(sketch, "E263.visualSharp", {"position": v(17.41, -190.55) * mm});
            skArc(sketch, "E263.filletArc", {"start": v(17.73, -190.48) * mm, "mid": v(17.42, -190.56) * mm, "end": v(17.1, -190.66) * mm});
            skPoint(sketch, "E264.visualSharp", {"position": v(-112.42, -236.4) * mm});
            skArc(sketch, "E264.filletArc", {"start": v(-111.18, -235.96) * mm, "mid": v(-112.35, -236.5) * mm, "end": v(-113.38, -237.28) * mm});
            skPoint(sketch, "E265.visualSharp", {"position": v(30.38, -26.54) * mm});
            skArc(sketch, "E265.filletArc", {"start": v(35.1, -28.5) * mm, "mid": v(30.89, -28.27) * mm, "end": v(27.46, -30.74) * mm});
            skPoint(sketch, "E266.visualSharp", {"position": v(33.94, 6.37) * mm});
            skArc(sketch, "E266.filletArc", {"start": v(32.9, 8.6) * mm, "mid": v(34.26, 6.7) * mm, "end": v(36.21, 5.43) * mm});
            skPoint(sketch, "E267.visualSharp", {"position": v(5.2, -7.13) * mm});
            skArc(sketch, "E267.filletArc", {"start": v(3.11, -10.14) * mm, "mid": v(4.23, -7.05) * mm, "end": v(3.65, -3.82) * mm});
            skPoint(sketch, "E268.visualSharp", {"position": v(-269.25, -93.57) * mm});
            skArc(sketch, "E268.filletArc", {"start": v(-270.05, -94.97) * mm, "mid": v(-269.45, -93.52) * mm, "end": v(-269.22, -91.96) * mm});
            skPoint(sketch, "E269.visualSharp", {"position": v(-265.58, 85.53) * mm});
            skArc(sketch, "E269.filletArc", {"start": v(-265.64, 82.49) * mm, "mid": v(-266.21, 85.24) * mm, "end": v(-267.92, 87.48) * mm});
            skPoint(sketch, "E270.visualSharp", {"position": v(-233.8, 86.7) * mm});
            skArc(sketch, "E270.filletArc", {"start": v(-230.9, 88.53) * mm, "mid": v(-233.05, 86.28) * mm, "end": v(-233.87, 83.27) * mm});
            skPoint(sketch, "E271.visualSharp", {"position": v(-250.09, 113.97) * mm});
            skArc(sketch, "E271.filletArc", {"start": v(-253.63, 116.93) * mm, "mid": v(-249.98, 115.46) * mm, "end": v(-246.18, 116.42) * mm});
            skPoint(sketch, "E272.visualSharp", {"position": v(-52.33, 115.6) * mm});
            skArc(sketch, "E272.filletArc", {"start": v(-50.99, 112.73) * mm, "mid": v(-52.8, 115) * mm, "end": v(-55.43, 116.24) * mm});
            skPoint(sketch, "E273.visualSharp", {"position": v(-153.61, 136.93) * mm});
            skArc(sketch, "E273.filletArc", {"start": v(-151.1, 136.4) * mm, "mid": v(-153.52, 136.44) * mm, "end": v(-155.78, 135.57) * mm});
            skPoint(sketch, "E274.visualSharp", {"position": v(-198.36, 146.37) * mm});
            skArc(sketch, "E274.filletArc", {"start": v(-211.7, 138.02) * mm, "mid": v(-208.82, 144.5) * mm, "end": v(-213.76, 149.61) * mm});
            skPoint(sketch, "E275.visualSharp", {"position": v(-46.95, 146.9) * mm});
            skArc(sketch, "E275.filletArc", {"start": v(-51.96, 147.96) * mm, "mid": v(-47.77, 148.51) * mm, "end": v(-44.85, 151.57) * mm});
            skPoint(sketch, "E276.visualSharp", {"position": v(-21.86, 125.4) * mm});
            skArc(sketch, "E276.filletArc", {"start": v(-20.65, 128.06) * mm, "mid": v(-21.22, 125.4) * mm, "end": v(-20.62, 122.74) * mm});
            skPoint(sketch, "E277.visualSharp", {"position": v(-319.2, 171.83) * mm});
            skArc(sketch, "E277.filletArc", {"start": v(-294.3, 166.59) * mm, "mid": v(-301.33, 163.15) * mm, "end": v(-299.7, 155.5) * mm});
            skPoint(sketch, "E278.visualSharp", {"position": v(-370.97, 215.2) * mm});
            skArc(sketch, "E278.filletArc", {"start": v(-372.19, 216.2) * mm, "mid": v(-370.89, 215.37) * mm, "end": v(-369.42, 214.86) * mm});
            skLineSegment(sketch, "E279", {"start": v(-529.45, 382.68) * mm, "end": v(-529.45, 309.45) * mm});
            skPoint(sketch, "E280.visualSharp", {"position": v(-529.45, 306.48) * mm});
            skArc(sketch, "E280.filletArc", {"start": v(-529.45, 309.45) * mm, "mid": v(-528.86, 306.76) * mm, "end": v(-527.18, 304.58) * mm});
            skPoint(sketch, "E281.visualSharp", {"position": v(-497.7, 321.3) * mm});
            skArc(sketch, "E281.filletArc", {"start": v(-497.7, 324.27) * mm, "mid": v(-497.1, 321.58) * mm, "end": v(-495.43, 319.4) * mm});
            skArc(sketch, "E282.MirrorCS", {"start": v(442.3, -94.97) * mm, "mid": v(441.7, -93.52) * mm, "end": v(441.48, -91.96) * mm});
            skArc(sketch, "E283.MirrorCS", {"start": v(403.15, 88.53) * mm, "mid": v(405.3, 86.28) * mm, "end": v(406.13, 83.27) * mm});
            skArc(sketch, "E284.MirrorCS", {"start": v(181.38, -164.82) * mm, "mid": v(179.3, -165.15) * mm, "end": v(177.24, -164.79) * mm});
            skArc(sketch, "E285.MirrorCS", {"start": v(163.58, -160) * mm, "mid": v(163.89, -160.09) * mm, "end": v(164.2, -160.19) * mm});
            skLineSegment(sketch, "E286.MirrorCS", {"start": v(177.24, -164.79) * mm, "end": v(164.2, -160.19) * mm});
            skArc(sketch, "E287.MirrorCS", {"start": v(437.9, 82.49) * mm, "mid": v(438.47, 85.24) * mm, "end": v(440.17, 87.48) * mm});
            skArc(sketch, "E288.MirrorCS", {"start": v(283.44, -235.96) * mm, "mid": v(284.6, -236.5) * mm, "end": v(285.63, -237.28) * mm});
            skLineSegment(sketch, "E289.MirrorCS", {"start": v(286.34, -197.4) * mm, "end": v(300.16, -169.6) * mm});
            skArc(sketch, "E290.MirrorCS", {"start": v(137.15, -28.5) * mm, "mid": v(141.37, -28.27) * mm, "end": v(144.8, -30.74) * mm});
            skArc(sketch, "E291.MirrorCS", {"start": v(154.53, -190.48) * mm, "mid": v(154.84, -190.56) * mm, "end": v(155.15, -190.66) * mm});
            skArc(sketch, "E292.MirrorCS", {"start": v(323.36, 136.4) * mm, "mid": v(325.78, 136.44) * mm, "end": v(328.04, 135.57) * mm});
            skArc(sketch, "E293.MirrorCS", {"start": v(286.34, -197.4) * mm, "mid": v(283.04, -200.46) * mm, "end": v(278.54, -200.56) * mm});
            skArc(sketch, "E294.MirrorCS", {"start": v(292.44, -160.76) * mm, "mid": v(299.26, -162.6) * mm, "end": v(300.16, -169.6) * mm});
            skArc(sketch, "E295.MirrorCS", {"start": v(544.45, 216.2) * mm, "mid": v(543.15, 215.37) * mm, "end": v(541.68, 214.86) * mm});
            skArc(sketch, "E296.MirrorCS", {"start": v(223.25, 112.73) * mm, "mid": v(225.05, 115) * mm, "end": v(227.69, 116.24) * mm});
            skArc(sketch, "E297.MirrorCS", {"start": v(669.96, 324.27) * mm, "mid": v(669.36, 321.58) * mm, "end": v(667.69, 319.4) * mm});
            skArc(sketch, "E298.MirrorCS", {"start": v(425.88, 116.93) * mm, "mid": v(422.24, 115.46) * mm, "end": v(418.44, 116.42) * mm});
            skArc(sketch, "E299.MirrorCS", {"start": v(348.48, -143.76) * mm, "mid": v(349.99, -141.8) * mm, "end": v(352.13, -140.57) * mm});
            skArc(sketch, "E300.MirrorCS", {"start": v(224.22, 147.96) * mm, "mid": v(220.03, 148.51) * mm, "end": v(217.11, 151.57) * mm});
            skArc(sketch, "E301.MirrorCS", {"start": v(139.35, 8.6) * mm, "mid": v(138, 6.7) * mm, "end": v(136.04, 5.43) * mm});
            skArc(sketch, "E302.MirrorCS", {"start": v(315.06, -221.23) * mm, "mid": v(313.12, -217.7) * mm, "end": v(313.68, -213.73) * mm});
            skArc(sketch, "E303.MirrorCS", {"start": v(263.13, -137.16) * mm, "mid": v(259.1, -137.18) * mm, "end": v(255.88, -134.77) * mm});
            skLineSegment(sketch, "E304.MirrorCS", {"start": v(418.44, 116.42) * mm, "end": v(383.95, 138.02) * mm});
            skArc(sketch, "E305.MirrorCS", {"start": v(192.9, 128.06) * mm, "mid": v(193.47, 125.4) * mm, "end": v(192.87, 122.74) * mm});
            skArc(sketch, "E306.MirrorCS", {"start": v(383.95, 138.02) * mm, "mid": v(381.07, 144.5) * mm, "end": v(386.02, 149.61) * mm});
            skArc(sketch, "E307.MirrorCS", {"start": v(409.56, -82.93) * mm, "mid": v(408.41, -86.71) * mm, "end": v(405.25, -89.08) * mm});
            skArc(sketch, "E308.MirrorCS", {"start": v(413.91, -119.67) * mm, "mid": v(418.2, -119.75) * mm, "end": v(421.47, -122.54) * mm});
            skArc(sketch, "E309.MirrorCS", {"start": v(701.71, 309.45) * mm, "mid": v(701.11, 306.76) * mm, "end": v(699.44, 304.58) * mm});
            skArc(sketch, "E310.MirrorCS", {"start": v(466.56, 166.59) * mm, "mid": v(473.59, 163.15) * mm, "end": v(471.95, 155.5) * mm});
            skLineSegment(sketch, "E311.MirrorCS", {"start": v(219.3, -152) * mm, "end": v(181.38, -164.82) * mm});
            skLineSegment(sketch, "E312.MirrorCS", {"start": v(701.71, -550.77) * mm, "end": v(625.51, -550.77) * mm});
            skLineSegment(sketch, "E313.MirrorCS", {"start": v(278.54, -200.56) * mm, "end": v(245.1, -188.75) * mm});
            skArc(sketch, "E314.MirrorCS", {"start": v(637.06, -501.36) * mm, "mid": v(635.49, -509.47) * mm, "end": v(627.23, -509.17) * mm});
            skLineSegment(sketch, "E315.MirrorCS", {"start": v(292.44, -160.76) * mm, "end": v(245.18, -176.75) * mm});
            skArc(sketch, "E316.MirrorCS", {"start": v(245.1, -188.75) * mm, "mid": v(240.87, -182.72) * mm, "end": v(245.18, -176.75) * mm});
            skArc(sketch, "E317.MirrorCS", {"start": v(222.47, -142.35) * mm, "mid": v(223.3, -147.96) * mm, "end": v(219.3, -152) * mm});
            skArc(sketch, "E318.MirrorCS", {"start": v(169.15, -10.14) * mm, "mid": v(168.03, -7.05) * mm, "end": v(168.6, -3.82) * mm});
            skLineSegment(sketch, "E319.MirrorCS", {"start": v(313.68, -213.73) * mm, "end": v(348.48, -143.76) * mm});
            skLineSegment(sketch, "E320.MirrorCS", {"start": v(164.17, 230.28) * mm, "end": v(146.57, 230.28) * mm});
            skLineSegment(sketch, "E321.MirrorCS", {"start": v(471.95, 155.5) * mm, "end": v(425.88, 116.93) * mm});
            skLineSegment(sketch, "E322.MirrorCS", {"start": v(669.96, 324.27) * mm, "end": v(669.96, 329.92) * mm});
            skLineSegment(sketch, "E323.MirrorCS", {"start": v(690.8, -550.77) * mm, "end": v(628, -550.77) * mm});
            skLineSegment(sketch, "E324.MirrorCS", {"start": v(136.04, 5.43) * mm, "end": v(122.58, -0.17) * mm});
            skPoint(sketch, "E325.MirrorP", {"position": v(179.3, -165.52) * mm});
            skLineSegment(sketch, "E326.MirrorCS", {"start": v(169.15, -10.14) * mm, "end": v(255.88, -134.77) * mm});
            skLineSegment(sketch, "E327.MirrorCS", {"start": v(466.56, 166.59) * mm, "end": v(386.02, 149.61) * mm});
            skPoint(sketch, "E328.MirrorP", {"position": v(307.01, -155.83) * mm});
            skPoint(sketch, "E329.MirrorP", {"position": v(141.88, -26.54) * mm});
            skPoint(sketch, "E330.MirrorP", {"position": v(370.62, 146.37) * mm});
            skPoint(sketch, "E331.MirrorP", {"position": v(406.06, 86.7) * mm});
            skLineSegment(sketch, "E332.MirrorCS", {"start": v(144.8, -30.74) * mm, "end": v(222.47, -142.35) * mm});
            skLineSegment(sketch, "E333.MirrorCS", {"start": v(413.91, -119.67) * mm, "end": v(352.13, -140.57) * mm});
            skLineSegment(sketch, "E334.MirrorCS", {"start": v(403.15, 88.53) * mm, "end": v(328.04, 135.57) * mm});
            skPoint(sketch, "E335.MirrorP", {"position": v(258.6, -138.7) * mm});
            skLineSegment(sketch, "E336.MirrorCS", {"start": v(163.58, -160) * mm, "end": v(122.59, -150.07) * mm});
            skLineSegment(sketch, "E337.MirrorCS", {"start": v(154.53, -190.48) * mm, "end": v(122.59, -182.74) * mm});
            skLineSegment(sketch, "E338.MirrorCS", {"start": v(405.25, -89.08) * mm, "end": v(263.13, -137.16) * mm});
            skPoint(sketch, "E339.MirrorP", {"position": v(669.96, 321.3) * mm});
            skPoint(sketch, "E340.MirrorP", {"position": v(224.6, 115.6) * mm});
            skPoint(sketch, "E341.MirrorP", {"position": v(167.05, -7.13) * mm});
            skPoint(sketch, "E342.MirrorP", {"position": v(219.2, 146.9) * mm});
            skLineSegment(sketch, "E343.MirrorCS", {"start": v(181.78, 230.28) * mm, "end": v(217.11, 151.57) * mm});
            skLineSegment(sketch, "E344.MirrorCS", {"start": v(627.23, -509.17) * mm, "end": v(315.06, -221.23) * mm});
            skLineSegment(sketch, "E345.MirrorCS", {"start": v(192.87, 122.74) * mm, "end": v(139.35, 8.6) * mm});
            skLineSegment(sketch, "E346.MirrorCS", {"start": v(406.13, 83.27) * mm, "end": v(409.55, -83.53) * mm});
            skLineSegment(sketch, "E347.MirrorCS", {"start": v(667.69, 319.4) * mm, "end": v(584, 249.33) * mm});
            skLineSegment(sketch, "E348.MirrorCS", {"start": v(701.71, 382.68) * mm, "end": v(701.71, 309.45) * mm});
            skPoint(sketch, "E349.MirrorP", {"position": v(227.78, -182.64) * mm});
            skPoint(sketch, "E350.MirrorP", {"position": v(422.35, 113.97) * mm});
            skLineSegment(sketch, "E351.MirrorCS", {"start": v(146.57, 230.28) * mm, "end": v(192.9, 128.06) * mm});
            skPoint(sketch, "E352.MirrorP", {"position": v(491.45, 171.83) * mm});
            skPoint(sketch, "E353.MirrorP", {"position": v(349.64, -141.4) * mm});
            skPoint(sketch, "E354.MirrorP", {"position": v(701.71, 306.48) * mm});
            skPoint(sketch, "E355.MirrorP", {"position": v(437.84, 85.53) * mm});
            skLineSegment(sketch, "E356.MirrorCS", {"start": v(421.47, -122.54) * mm, "end": v(637.06, -501.36) * mm});
            skPoint(sketch, "E357.MirrorP", {"position": v(227.3, -149.28) * mm});
            skLineSegment(sketch, "E358.MirrorCS", {"start": v(541.68, 214.86) * mm, "end": v(224.22, 147.96) * mm});
            skPoint(sketch, "E359.MirrorP", {"position": v(543.23, 215.2) * mm});
            skLineSegment(sketch, "E360.MirrorCS", {"start": v(699.44, 304.58) * mm, "end": v(440.17, 87.48) * mm});
            skPoint(sketch, "E361.MirrorP", {"position": v(283.84, -202.43) * mm});
            skPoint(sketch, "E362.MirrorP", {"position": v(154.84, -190.55) * mm});
            skLineSegment(sketch, "E363.MirrorCS", {"start": v(283.44, -235.96) * mm, "end": v(155.15, -190.66) * mm});
            skPoint(sketch, "E364.MirrorP", {"position": v(325.87, 136.93) * mm});
            skPoint(sketch, "E365.MirrorP", {"position": v(194.12, 125.4) * mm});
            skLineSegment(sketch, "E366.MirrorCS", {"start": v(623.69, -549.09) * mm, "end": v(285.63, -237.28) * mm});
            skLineSegment(sketch, "E367.MirrorCS", {"start": v(442.3, -94.97) * mm, "end": v(696.3, -541.28) * mm});
            skPoint(sketch, "E368.MirrorP", {"position": v(418.88, -117.99) * mm});
            skLineSegment(sketch, "E369.MirrorCS", {"start": v(223.25, 112.73) * mm, "end": v(168.6, -3.82) * mm});
            skPoint(sketch, "E370.MirrorP", {"position": v(138.32, 6.37) * mm});
            skPoint(sketch, "E371.MirrorP", {"position": v(163.9, -160.08) * mm});
            skPoint(sketch, "E372.MirrorP", {"position": v(284.67, -236.4) * mm});
            skPoint(sketch, "E373.MirrorP", {"position": v(311.55, -218) * mm});
            skPoint(sketch, "E374.MirrorP", {"position": v(409.66, -87.59) * mm});
            skLineSegment(sketch, "E375.MirrorCS", {"start": v(437.9, 82.49) * mm, "end": v(441.48, -91.96) * mm});
            skLineSegment(sketch, "E376.MirrorCS", {"start": v(323.36, 136.4) * mm, "end": v(227.69, 116.24) * mm});
            skPoint(sketch, "E377.MirrorP", {"position": v(441.51, -93.57) * mm});
            skLineSegment(sketch, "E378", {"start": v(-478.65, 363.63) * mm, "end": v(-478.65, 348.25) * mm});
            skLineSegment(sketch, "E379", {"start": v(-481.83, 342.75) * mm, "end": v(-494.53, 335.41) * mm});
            skLineSegment(sketch, "E380.trimOffspring", {"start": v(-497.7, 363.63) * mm, "end": v(-497.7, 382.68) * mm});
            skPoint(sketch, "E381.visualSharp", {"position": v(-497.7, 333.58) * mm});
            skArc(sketch, "E381.filletArc", {"start": v(-494.53, 335.41) * mm, "mid": v(-496.85, 333.1) * mm, "end": v(-497.7, 329.92) * mm});
            skPoint(sketch, "E382.visualSharp", {"position": v(-478.65, 344.58) * mm});
            skArc(sketch, "E382.filletArc", {"start": v(-481.83, 342.75) * mm, "mid": v(-479.5, 345.07) * mm, "end": v(-478.65, 348.25) * mm});
            skLineSegment(sketch, "E383.trimOffspring", {"start": v(669.96, 382.68) * mm, "end": v(701.71, 382.68) * mm});
            skLineSegment(sketch, "E384", {"start": v(25.68, 230.28) * mm, "end": v(25.68, 249.33) * mm});
            skLineSegment(sketch, "E385", {"start": v(8.08, 249.33) * mm, "end": v(-9.52, 249.33) * mm});
            skLineSegment(sketch, "E386", {"start": v(-9.52, 249.33) * mm, "end": v(-9.52, 230.28) * mm});
            skLineSegment(sketch, "E387", {"start": v(146.57, 230.28) * mm, "end": v(146.57, 249.33) * mm});
            skLineSegment(sketch, "E388", {"start": v(164.17, 249.33) * mm, "end": v(181.78, 249.33) * mm});
            skLineSegment(sketch, "E389", {"start": v(181.78, 249.33) * mm, "end": v(181.78, 230.28) * mm});
            skLineSegment(sketch, "E390", {"start": v(669.96, 363.63) * mm, "end": v(650.91, 363.63) * mm});
            skLineSegment(sketch, "E391", {"start": v(650.91, 363.63) * mm, "end": v(650.91, 348.25) * mm});
            skLineSegment(sketch, "E392", {"start": v(654.09, 342.75) * mm, "end": v(666.79, 335.41) * mm});
            skLineSegment(sketch, "E393.trimOffspring", {"start": v(669.96, 363.63) * mm, "end": v(669.96, 382.68) * mm});
            skPoint(sketch, "E394.visualSharp", {"position": v(650.91, 344.58) * mm});
            skArc(sketch, "E394.filletArc", {"start": v(650.91, 348.25) * mm, "mid": v(651.76, 345.07) * mm, "end": v(654.09, 342.75) * mm});
            skPoint(sketch, "E395.visualSharp", {"position": v(669.96, 333.58) * mm});
            skArc(sketch, "E395.filletArc", {"start": v(669.96, 329.92) * mm, "mid": v(669.1, 333.1) * mm, "end": v(666.79, 335.41) * mm});
            skPoint(sketch, "E396.visualSharp", {"position": v(625.51, -550.77) * mm});
            skArc(sketch, "E396.filletArc", {"start": v(623.69, -549.09) * mm, "mid": v(625.68, -550.33) * mm, "end": v(628, -550.77) * mm});
            skPoint(sketch, "E397.visualSharp", {"position": v(701.71, -550.77) * mm});
            skArc(sketch, "E397.filletArc", {"start": v(690.8, -550.77) * mm, "mid": v(696.28, -547.61) * mm, "end": v(696.3, -541.28) * mm});
            skPoint(sketch, "E398.visualSharp", {"position": v(-529.45, -550.77) * mm});
            skArc(sketch, "E398.filletArc", {"start": v(-524.05, -541.28) * mm, "mid": v(-524.02, -547.61) * mm, "end": v(-518.53, -550.77) * mm});
            skPoint(sketch, "E399.visualSharp", {"position": v(-453.25, -550.77) * mm});
            skArc(sketch, "E399.filletArc", {"start": v(-455.73, -550.77) * mm, "mid": v(-453.42, -550.33) * mm, "end": v(-451.43, -549.09) * mm});
            skLineSegment(sketch, "E400", {"start": v(86.13, -0.17) * mm, "end": v(86.13, -34.56) * mm, "construction": true});
            skLineSegment(sketch, "E401", {"start": v(86.13, -150.07) * mm, "end": v(86.13, -182.74) * mm, "construction": true});
            skLineSegment(sketch, "E402", {"start": v(137.15, -28.5) * mm, "end": v(122.59, -34.56) * mm});
            skLineSegment(sketch, "E403", {"start": v(109.25, -34.56) * mm, "end": v(109.25, -17.36) * mm});
            skLineSegment(sketch, "E404", {"start": v(63, -34.56) * mm, "end": v(49.67, -34.56) * mm});
            skLineSegment(sketch, "E405", {"start": v(76.6, -0.17) * mm, "end": v(49.67, -0.17) * mm});
            skLineSegment(sketch, "E406", {"start": v(35.1, -28.5) * mm, "end": v(49.67, -34.56) * mm});
            skPoint(sketch, "E407", {"position": v(122.58, -17.36) * mm});
            skLineSegment(sketch, "E408", {"start": v(90.2, -17.36) * mm, "end": v(82.06, -17.36) * mm});
            skLineSegment(sketch, "E409", {"start": v(63.01, -182.74) * mm, "end": v(49.67, -182.74) * mm});
            skLineSegment(sketch, "E410", {"start": v(63, -150.07) * mm, "end": v(49.67, -150.07) * mm});
            skPoint(sketch, "E411", {"position": v(122.59, -166.4) * mm});
            skLineSegment(sketch, "E412", {"start": v(584, 249.33) * mm, "end": v(584, 230.28) * mm});
            skLineSegment(sketch, "E413.trimOffspring", {"start": v(561.25, 230.28) * mm, "end": v(544.45, 216.2) * mm});
            skLineSegment(sketch, "E414", {"start": v(584, 230.28) * mm, "end": v(561.25, 230.28) * mm});
            skLineSegment(sketch, "E415", {"start": v(-411.75, 249.33) * mm, "end": v(-411.75, 230.28) * mm});
            skLineSegment(sketch, "E416", {"start": v(-411.75, 230.28) * mm, "end": v(-389, 230.28) * mm});
            skLineSegment(sketch, "E417.trimOffspring", {"start": v(-389, 230.28) * mm, "end": v(-372.19, 216.2) * mm});
            skPoint(sketch, "E418", {"position": v(164.17, 249.33) * mm});
            skPoint(sketch, "E419", {"position": v(8.08, 249.33) * mm});
            skLineSegment(sketch, "E420.0", {"start": v(141.72, 249.33) * mm, "end": v(256.02, 363.63) * mm});
            skLineSegment(sketch, "E421", {"start": v(300.93, 363.63) * mm, "end": v(300.93, 382.68) * mm});
            skLineSegment(sketch, "E422", {"start": v(256.02, 363.63) * mm, "end": v(256.02, 382.68) * mm});
            skLineSegment(sketch, "E423", {"start": v(256.02, 382.68) * mm, "end": v(300.93, 382.68) * mm});
            skLineSegment(sketch, "E424", {"start": v(141.72, 249.33) * mm, "end": v(146.57, 249.33) * mm});
            skLineSegment(sketch, "E425", {"start": v(181.78, 249.33) * mm, "end": v(186.63, 249.33) * mm});
            skLineSegment(sketch, "E426.trimOffspring", {"start": v(186.63, 249.33) * mm, "end": v(300.93, 363.63) * mm});
            skLineSegment(sketch, "E427", {"start": v(164.17, 249.33) * mm, "end": v(164.17, 230.28) * mm});
            skLineSegment(sketch, "E428.trimOffspring", {"start": v(146.57, 249.33) * mm, "end": v(25.68, 249.33) * mm, "construction": true});
            skLineSegment(sketch, "E429.0", {"start": v(-14.37, 249.33) * mm, "end": v(-128.67, 363.63) * mm});
            skLineSegment(sketch, "E430.0", {"start": v(30.53, 249.33) * mm, "end": v(-83.77, 363.63) * mm});
            skLineSegment(sketch, "E431", {"start": v(30.53, 249.33) * mm, "end": v(25.68, 249.33) * mm});
            skLineSegment(sketch, "E432", {"start": v(-9.52, 249.33) * mm, "end": v(-14.37, 249.33) * mm});
            skLineSegment(sketch, "E433", {"start": v(-128.67, 363.63) * mm, "end": v(-128.67, 382.68) * mm});
            skLineSegment(sketch, "E434", {"start": v(-83.77, 363.63) * mm, "end": v(-83.77, 382.68) * mm});
            skLineSegment(sketch, "E435", {"start": v(-83.77, 382.68) * mm, "end": v(-128.67, 382.68) * mm});
            skLineSegment(sketch, "E436", {"start": v(49.67, -150.07) * mm, "end": v(49.67, -182.74) * mm, "construction": true});
            skLineSegment(sketch, "E437", {"start": v(49.67, -0.17) * mm, "end": v(49.67, -34.56) * mm, "construction": true});
            skLineSegment(sketch, "E438", {"start": v(8.08, 249.33) * mm, "end": v(8.08, 230.28) * mm});
            skPoint(sketch, "E439.orphan", {"position": v(122.58, -34.56) * mm});
            skLineSegment(sketch, "E440", {"start": v(122.58, -0.17) * mm, "end": v(76.6, -0.17) * mm});
            skLineSegment(sketch, "E441", {"start": v(109.25, -150.07) * mm, "end": v(122.59, -150.07) * mm});
            skLineSegment(sketch, "E442", {"start": v(122.59, -182.74) * mm, "end": v(109.25, -182.74) * mm});
            skLineSegment(sketch, "E443", {"start": v(63, -34.56) * mm, "end": v(63, -17.36) * mm});
            skLineSegment(sketch, "E444", {"start": v(122.59, -34.56) * mm, "end": v(109.25, -34.56) * mm});
            skLineSegment(sketch, "E445.trimOffspring", {"start": v(63, -0.17) * mm, "end": v(63, 0) * mm});
            skLineSegment(sketch, "E446", {"start": v(63, -150.07) * mm, "end": v(72.53, -150.07) * mm});
            skPoint(sketch, "E447.orphan", {"position": v(82.06, -150.07) * mm});
            skLineSegment(sketch, "E448", {"start": v(63.01, -182.74) * mm, "end": v(82.06, -182.74) * mm});
            skLineSegment(sketch, "E449", {"start": v(82.06, -182.74) * mm, "end": v(82.06, -150.07) * mm});
            skLineSegment(sketch, "E450", {"start": v(82.06, -150.07) * mm, "end": v(63, -150.07) * mm});
            skLineSegment(sketch, "E451", {"start": v(109.25, -150.07) * mm, "end": v(90.2, -150.07) * mm});
            skLineSegment(sketch, "E452", {"start": v(90.2, -150.07) * mm, "end": v(90.2, -182.74) * mm});
            skLineSegment(sketch, "E453", {"start": v(109.25, -182.74) * mm, "end": v(90.2, -182.74) * mm});
            skLineSegment(sketch, "E454", {"start": v(82.06, -34.56) * mm, "end": v(82.06, -17.36) * mm});
            skLineSegment(sketch, "E455", {"start": v(90.2, -34.56) * mm, "end": v(90.2, -17.36) * mm});
            skLineSegment(sketch, "E456", {"start": v(63, -34.56) * mm, "end": v(82.06, -34.56) * mm});
            skLineSegment(sketch, "E457.trimOffspring", {"start": v(90.2, -34.56) * mm, "end": v(109.25, -34.56) * mm});
            skSolve(sketch);
        }
        {
            var Q0;
            Q0=qCreatedBy(makeId("Front.planeOp"),FACE);
            var sketch = newSketch(context, id + "F5", { "sketchPlane" : qUnion([Q0])});
            skLineSegment(sketch, "E458.bottom", {"start": v(-726.25, -550.77) * mm, "end": v(-663.45, -550.77) * mm});
            skLineSegment(sketch, "E458.top", {"start": v(-737.17, 382.68) * mm, "end": v(-705.42, 382.68) * mm});
            skLineSegment(sketch, "E459", {"start": v(-705.42, 363.63) * mm, "end": v(-686.37, 363.63) * mm});
            skLineSegment(sketch, "E460", {"start": v(-734.9, 304.57) * mm, "end": v(-475.64, 87.48) * mm});
            skLineSegment(sketch, "E461", {"start": v(-473.37, 82.48) * mm, "end": v(-476.94, -91.96) * mm});
            skLineSegment(sketch, "E462", {"start": v(-477.77, -94.97) * mm, "end": v(-731.77, -541.28) * mm});
            skLineSegment(sketch, "E463", {"start": v(-726.25, -550.77) * mm, "end": v(-660.97, -550.77) * mm});
            skLineSegment(sketch, "E464", {"start": v(-659.15, -549.1) * mm, "end": v(-321.1, -237.28) * mm});
            skLineSegment(sketch, "E465", {"start": v(-318.9, -235.96) * mm, "end": v(-190.61, -190.66) * mm});
            skLineSegment(sketch, "E466", {"start": v(-190, -190.48) * mm, "end": v(-158.05, -182.74) * mm});
            skLineSegment(sketch, "E467", {"start": v(-181, 230.29) * mm, "end": v(-227.34, 128.07) * mm});
            skLineSegment(sketch, "E468", {"start": v(-227.31, 122.75) * mm, "end": v(-173.8, 8.6) * mm});
            skLineSegment(sketch, "E469", {"start": v(-170.48, 5.43) * mm, "end": v(-157.02, -0.16) * mm});
            skLineSegment(sketch, "E470.0", {"start": v(-662.7, -509.17) * mm, "end": v(-350.52, -221.23) * mm});
            skLineSegment(sketch, "E471.0", {"start": v(-456.93, -122.54) * mm, "end": v(-672.52, -501.36) * mm});
            skLineSegment(sketch, "E472.0", {"start": v(-199.04, -160) * mm, "end": v(-158.05, -150.07) * mm});
            skLineSegment(sketch, "E472.1", {"start": v(-314, -200.56) * mm, "end": v(-280.57, -188.76) * mm});
            skLineSegment(sketch, "E473.1", {"start": v(-258.71, 112.72) * mm, "end": v(-204.07, -3.82) * mm});
            skLineSegment(sketch, "E474.0", {"start": v(-705.42, 324.27) * mm, "end": v(-705.42, 329.91) * mm});
            skLineSegment(sketch, "E475.0", {"start": v(-703.15, 319.4) * mm, "end": v(-619.47, 249.33) * mm});
            skLineSegment(sketch, "E476.0", {"start": v(-441.6, 83.27) * mm, "end": v(-445.01, -83.54) * mm});
            skLineSegment(sketch, "E477.0", {"start": v(-502.03, 166.58) * mm, "end": v(-421.48, 149.6) * mm});
            skLineSegment(sketch, "E478.0", {"start": v(-577.14, 214.86) * mm, "end": v(-259.68, 147.96) * mm});
            skLineSegment(sketch, "E479.0", {"start": v(-438.61, 88.52) * mm, "end": v(-363.5, 135.57) * mm});
            skLineSegment(sketch, "E480.0", {"start": v(-453.9, 116.41) * mm, "end": v(-419.42, 138.01) * mm});
            skLineSegment(sketch, "E481.0", {"start": v(-440.71, -89.08) * mm, "end": v(-298.6, -137.16) * mm});
            skLineSegment(sketch, "E482.0", {"start": v(-449.38, -119.67) * mm, "end": v(-387.59, -140.57) * mm});
            skLineSegment(sketch, "E483.0", {"start": v(-321.8, -197.4) * mm, "end": v(-335.62, -169.6) * mm});
            skLineSegment(sketch, "E484.0", {"start": v(-349.14, -213.73) * mm, "end": v(-383.94, -143.76) * mm});
            skLineSegment(sketch, "E485.0", {"start": v(-204.6, -10.14) * mm, "end": v(-291.34, -134.78) * mm});
            skLineSegment(sketch, "E486.0", {"start": v(-180.26, -30.74) * mm, "end": v(-257.93, -142.35) * mm});
            skLineSegment(sketch, "E487.trimOffspring", {"start": v(-507.41, 155.5) * mm, "end": v(-461.35, 116.93) * mm});
            skLineSegment(sketch, "E488.trimOffspring", {"start": v(-358.82, 136.4) * mm, "end": v(-263.15, 116.24) * mm});
            skLineSegment(sketch, "E489.trimOffspring", {"start": v(-254.76, -152) * mm, "end": v(-216.85, -164.82) * mm});
            skLineSegment(sketch, "E490.trimOffspring", {"start": v(-327.9, -160.77) * mm, "end": v(-280.65, -176.75) * mm});
            skLineSegment(sketch, "E491", {"start": v(-199.64, 230.29) * mm, "end": v(-181, 230.29) * mm});
            skPoint(sketch, "E492.orphan", {"position": v(-120.56, 363.64) * mm});
            skLineSegment(sketch, "E493.trimOffspring", {"start": v(-218.27, 230.29) * mm, "end": v(-252.55, 151.63) * mm});
            skPoint(sketch, "E494.visualSharp", {"position": v(-319.3, -202.43) * mm});
            skArc(sketch, "E494.filletArc", {"start": v(-321.8, -197.4) * mm, "mid": v(-318.5, -200.46) * mm, "end": v(-314, -200.56) * mm});
            skLineSegment(sketch, "E495.trimOffspring", {"start": v(-212.7, -164.8) * mm, "end": v(-199.66, -160.19) * mm});
            skPoint(sketch, "E496.visualSharp", {"position": v(-342.47, -155.84) * mm});
            skArc(sketch, "E496.filletArc", {"start": v(-327.9, -160.77) * mm, "mid": v(-334.72, -162.6) * mm, "end": v(-335.62, -169.6) * mm});
            skPoint(sketch, "E497.visualSharp", {"position": v(-263.25, -182.64) * mm});
            skArc(sketch, "E497.filletArc", {"start": v(-280.57, -188.76) * mm, "mid": v(-276.33, -182.73) * mm, "end": v(-280.65, -176.75) * mm});
            skPoint(sketch, "E498.visualSharp", {"position": v(-347.02, -218) * mm});
            skArc(sketch, "E498.filletArc", {"start": v(-350.52, -221.23) * mm, "mid": v(-348.58, -217.71) * mm, "end": v(-349.14, -213.73) * mm});
            skPoint(sketch, "E499.visualSharp", {"position": v(-385.1, -141.41) * mm});
            skArc(sketch, "E499.filletArc", {"start": v(-383.94, -143.76) * mm, "mid": v(-385.45, -141.8) * mm, "end": v(-387.59, -140.57) * mm});
            skPoint(sketch, "E500.visualSharp", {"position": v(-454.34, -117.99) * mm});
            skArc(sketch, "E500.filletArc", {"start": v(-449.38, -119.67) * mm, "mid": v(-453.67, -119.75) * mm, "end": v(-456.93, -122.54) * mm});
            skPoint(sketch, "E501.visualSharp", {"position": v(-692.73, -536.87) * mm});
            skArc(sketch, "E501.filletArc", {"start": v(-672.52, -501.36) * mm, "mid": v(-670.95, -509.47) * mm, "end": v(-662.7, -509.17) * mm});
            skPoint(sketch, "E502.visualSharp", {"position": v(-445.12, -87.59) * mm});
            skArc(sketch, "E502.filletArc", {"start": v(-445.03, -82.94) * mm, "mid": v(-443.88, -86.71) * mm, "end": v(-440.71, -89.08) * mm});
            skPoint(sketch, "E503.visualSharp", {"position": v(-294.07, -138.7) * mm});
            skArc(sketch, "E503.filletArc", {"start": v(-298.6, -137.16) * mm, "mid": v(-294.57, -137.18) * mm, "end": v(-291.34, -134.78) * mm});
            skPoint(sketch, "E504.visualSharp", {"position": v(-262.76, -149.29) * mm});
            skArc(sketch, "E504.filletArc", {"start": v(-257.93, -142.35) * mm, "mid": v(-258.75, -147.97) * mm, "end": v(-254.76, -152) * mm});
            skPoint(sketch, "E505.visualSharp", {"position": v(-214.77, -165.52) * mm});
            skArc(sketch, "E505.filletArc", {"start": v(-216.85, -164.82) * mm, "mid": v(-214.77, -165.15) * mm, "end": v(-212.7, -164.8) * mm});
            skPoint(sketch, "E506.visualSharp", {"position": v(-199.36, -160.08) * mm});
            skArc(sketch, "E506.filletArc", {"start": v(-199.04, -160) * mm, "mid": v(-199.35, -160.09) * mm, "end": v(-199.66, -160.19) * mm});
            skPoint(sketch, "E507.visualSharp", {"position": v(-190.3, -190.56) * mm});
            skArc(sketch, "E507.filletArc", {"start": v(-190, -190.48) * mm, "mid": v(-190.3, -190.57) * mm, "end": v(-190.61, -190.66) * mm});
            skPoint(sketch, "E508.visualSharp", {"position": v(-320.14, -236.4) * mm});
            skArc(sketch, "E508.filletArc", {"start": v(-318.9, -235.96) * mm, "mid": v(-320.07, -236.51) * mm, "end": v(-321.1, -237.28) * mm});
            skPoint(sketch, "E509.visualSharp", {"position": v(-177.34, -26.54) * mm});
            skArc(sketch, "E509.filletArc", {"start": v(-172.61, -28.5) * mm, "mid": v(-176.83, -28.27) * mm, "end": v(-180.26, -30.74) * mm});
            skPoint(sketch, "E510.visualSharp", {"position": v(-172.75, 6.37) * mm});
            skArc(sketch, "E510.filletArc", {"start": v(-173.8, 8.6) * mm, "mid": v(-172.43, 6.7) * mm, "end": v(-170.48, 5.43) * mm});
            skPoint(sketch, "E511.visualSharp", {"position": v(-202.52, -7.14) * mm});
            skArc(sketch, "E511.filletArc", {"start": v(-204.6, -10.14) * mm, "mid": v(-203.5, -7.05) * mm, "end": v(-204.07, -3.82) * mm});
            skPoint(sketch, "E512.visualSharp", {"position": v(-476.97, -93.57) * mm});
            skArc(sketch, "E512.filletArc", {"start": v(-477.77, -94.97) * mm, "mid": v(-477.17, -93.52) * mm, "end": v(-476.94, -91.96) * mm});
            skPoint(sketch, "E513.visualSharp", {"position": v(-473.3, 85.53) * mm});
            skArc(sketch, "E513.filletArc", {"start": v(-473.37, 82.48) * mm, "mid": v(-473.93, 85.24) * mm, "end": v(-475.64, 87.48) * mm});
            skPoint(sketch, "E514.visualSharp", {"position": v(-441.52, 86.7) * mm});
            skArc(sketch, "E514.filletArc", {"start": v(-438.61, 88.52) * mm, "mid": v(-440.77, 86.27) * mm, "end": v(-441.6, 83.27) * mm});
            skPoint(sketch, "E515.visualSharp", {"position": v(-457.8, 113.96) * mm});
            skArc(sketch, "E515.filletArc", {"start": v(-461.35, 116.93) * mm, "mid": v(-457.7, 115.46) * mm, "end": v(-453.9, 116.41) * mm});
            skPoint(sketch, "E516.visualSharp", {"position": v(-260.05, 115.59) * mm});
            skArc(sketch, "E516.filletArc", {"start": v(-258.71, 112.72) * mm, "mid": v(-260.52, 115) * mm, "end": v(-263.15, 116.24) * mm});
            skPoint(sketch, "E517.visualSharp", {"position": v(-361.33, 136.93) * mm});
            skArc(sketch, "E517.filletArc", {"start": v(-358.82, 136.4) * mm, "mid": v(-361.25, 136.44) * mm, "end": v(-363.5, 135.57) * mm});
            skPoint(sketch, "E518.visualSharp", {"position": v(-406.09, 146.36) * mm});
            skArc(sketch, "E518.filletArc", {"start": v(-419.42, 138.01) * mm, "mid": v(-416.54, 144.5) * mm, "end": v(-421.48, 149.6) * mm});
            skPoint(sketch, "E519.visualSharp", {"position": v(-254.62, 146.89) * mm});
            skArc(sketch, "E519.filletArc", {"start": v(-259.68, 147.96) * mm, "mid": v(-255.46, 148.53) * mm, "end": v(-252.55, 151.63) * mm});
            skPoint(sketch, "E520.visualSharp", {"position": v(-228.55, 125.4) * mm});
            skArc(sketch, "E520.filletArc", {"start": v(-227.34, 128.07) * mm, "mid": v(-227.91, 125.4) * mm, "end": v(-227.31, 122.75) * mm});
            skPoint(sketch, "E521.visualSharp", {"position": v(-526.91, 171.83) * mm});
            skArc(sketch, "E521.filletArc", {"start": v(-502.03, 166.58) * mm, "mid": v(-509.05, 163.14) * mm, "end": v(-507.41, 155.5) * mm});
            skPoint(sketch, "E522.visualSharp", {"position": v(-578.7, 215.19) * mm});
            skArc(sketch, "E522.filletArc", {"start": v(-579.91, 216.2) * mm, "mid": v(-578.6, 215.36) * mm, "end": v(-577.14, 214.86) * mm});
            skLineSegment(sketch, "E523", {"start": v(-737.17, 382.68) * mm, "end": v(-737.17, 309.44) * mm});
            skPoint(sketch, "E524.visualSharp", {"position": v(-737.17, 306.48) * mm});
            skArc(sketch, "E524.filletArc", {"start": v(-737.17, 309.44) * mm, "mid": v(-736.58, 306.76) * mm, "end": v(-734.9, 304.57) * mm});
            skPoint(sketch, "E525.visualSharp", {"position": v(-705.42, 321.3) * mm});
            skArc(sketch, "E525.filletArc", {"start": v(-705.42, 324.27) * mm, "mid": v(-704.83, 321.58) * mm, "end": v(-703.15, 319.4) * mm});
            skArc(sketch, "E526.MirrorCS", {"start": v(234.59, -94.97) * mm, "mid": v(233.98, -93.52) * mm, "end": v(233.76, -91.96) * mm});
            skArc(sketch, "E527.MirrorCS", {"start": v(195.43, 88.52) * mm, "mid": v(197.58, 86.27) * mm, "end": v(198.4, 83.27) * mm});
            skArc(sketch, "E528.MirrorCS", {"start": v(-26.34, -164.82) * mm, "mid": v(-28.41, -165.15) * mm, "end": v(-30.49, -164.8) * mm});
            skArc(sketch, "E529.MirrorCS", {"start": v(-44.14, -160) * mm, "mid": v(-43.83, -160.09) * mm, "end": v(-43.52, -160.19) * mm});
            skLineSegment(sketch, "E530.MirrorCS", {"start": v(-30.49, -164.8) * mm, "end": v(-43.52, -160.19) * mm});
            skArc(sketch, "E531.MirrorCS", {"start": v(230.18, 82.48) * mm, "mid": v(230.75, 85.24) * mm, "end": v(232.45, 87.48) * mm});
            skArc(sketch, "E532.MirrorCS", {"start": v(75.72, -235.96) * mm, "mid": v(76.88, -236.51) * mm, "end": v(77.91, -237.28) * mm});
            skLineSegment(sketch, "E533.MirrorCS", {"start": v(78.62, -197.4) * mm, "end": v(92.44, -169.6) * mm});
            skArc(sketch, "E534.MirrorCS", {"start": v(-70.57, -28.5) * mm, "mid": v(-66.35, -28.27) * mm, "end": v(-62.92, -30.74) * mm});
            skArc(sketch, "E535.MirrorCS", {"start": v(-53.2, -190.48) * mm, "mid": v(-52.88, -190.57) * mm, "end": v(-52.57, -190.66) * mm});
            skArc(sketch, "E536.MirrorCS", {"start": v(115.64, 136.4) * mm, "mid": v(118.06, 136.44) * mm, "end": v(120.32, 135.57) * mm});
            skArc(sketch, "E537.MirrorCS", {"start": v(78.62, -197.4) * mm, "mid": v(75.32, -200.46) * mm, "end": v(70.82, -200.56) * mm});
            skArc(sketch, "E538.MirrorCS", {"start": v(84.72, -160.77) * mm, "mid": v(91.54, -162.6) * mm, "end": v(92.44, -169.6) * mm});
            skArc(sketch, "E539.MirrorCS", {"start": v(336.73, 216.2) * mm, "mid": v(335.43, 215.36) * mm, "end": v(333.96, 214.86) * mm});
            skArc(sketch, "E540.MirrorCS", {"start": v(15.53, 112.72) * mm, "mid": v(17.33, 115) * mm, "end": v(19.97, 116.24) * mm});
            skArc(sketch, "E541.MirrorCS", {"start": v(462.24, 324.27) * mm, "mid": v(461.64, 321.58) * mm, "end": v(459.97, 319.4) * mm});
            skArc(sketch, "E542.MirrorCS", {"start": v(218.16, 116.93) * mm, "mid": v(214.52, 115.46) * mm, "end": v(210.71, 116.41) * mm});
            skArc(sketch, "E543.MirrorCS", {"start": v(140.75, -143.76) * mm, "mid": v(142.26, -141.8) * mm, "end": v(144.4, -140.57) * mm});
            skArc(sketch, "E544.MirrorCS", {"start": v(16.5, 147.96) * mm, "mid": v(12.3, 148.5) * mm, "end": v(9.4, 151.57) * mm});
            skArc(sketch, "E545.MirrorCS", {"start": v(-66.8, 8.6) * mm, "mid": v(-68.15, 6.7) * mm, "end": v(-70.1, 5.43) * mm});
            skArc(sketch, "E546.MirrorCS", {"start": v(107.33, -221.23) * mm, "mid": v(105.4, -217.71) * mm, "end": v(105.95, -213.73) * mm});
            skArc(sketch, "E547.MirrorCS", {"start": v(55.4, -137.16) * mm, "mid": v(51.38, -137.18) * mm, "end": v(48.16, -134.78) * mm});
            skLineSegment(sketch, "E548.MirrorCS", {"start": v(210.71, 116.41) * mm, "end": v(176.23, 138.01) * mm});
            skArc(sketch, "E549.MirrorCS", {"start": v(-13.24, 128.07) * mm, "mid": v(-12.68, 125.4) * mm, "end": v(-13.28, 122.75) * mm});
            skArc(sketch, "E550.MirrorCS", {"start": v(176.23, 138.01) * mm, "mid": v(173.35, 144.5) * mm, "end": v(178.3, 149.6) * mm});
            skArc(sketch, "E551.MirrorCS", {"start": v(201.84, -82.94) * mm, "mid": v(200.7, -86.71) * mm, "end": v(197.53, -89.08) * mm});
            skArc(sketch, "E552.MirrorCS", {"start": v(206.2, -119.67) * mm, "mid": v(210.48, -119.75) * mm, "end": v(213.75, -122.54) * mm});
            skArc(sketch, "E553.MirrorCS", {"start": v(493.99, 309.44) * mm, "mid": v(493.4, 306.76) * mm, "end": v(491.72, 304.57) * mm});
            skArc(sketch, "E554.MirrorCS", {"start": v(258.84, 166.58) * mm, "mid": v(265.86, 163.14) * mm, "end": v(264.23, 155.5) * mm});
            skLineSegment(sketch, "E555.MirrorCS", {"start": v(11.57, -152) * mm, "end": v(-26.34, -164.82) * mm});
            skLineSegment(sketch, "E556.MirrorCS", {"start": v(493.99, -550.77) * mm, "end": v(417.79, -550.77) * mm});
            skLineSegment(sketch, "E557.MirrorCS", {"start": v(70.82, -200.56) * mm, "end": v(37.38, -188.76) * mm});
            skArc(sketch, "E558.MirrorCS", {"start": v(429.34, -501.36) * mm, "mid": v(427.77, -509.47) * mm, "end": v(419.51, -509.17) * mm});
            skLineSegment(sketch, "E559.MirrorCS", {"start": v(84.72, -160.77) * mm, "end": v(37.46, -176.75) * mm});
            skArc(sketch, "E560.MirrorCS", {"start": v(37.38, -188.76) * mm, "mid": v(33.15, -182.73) * mm, "end": v(37.46, -176.75) * mm});
            skArc(sketch, "E561.MirrorCS", {"start": v(14.75, -142.35) * mm, "mid": v(15.57, -147.97) * mm, "end": v(11.57, -152) * mm});
            skArc(sketch, "E562.MirrorCS", {"start": v(-38.58, -10.14) * mm, "mid": v(-39.7, -7.05) * mm, "end": v(-39.11, -3.82) * mm});
            skLineSegment(sketch, "E563.MirrorCS", {"start": v(105.95, -213.73) * mm, "end": v(140.75, -143.76) * mm});
            skLineSegment(sketch, "E564.MirrorCS", {"start": v(-42.76, 230.28) * mm, "end": v(-59.58, 230.29) * mm});
            skLineSegment(sketch, "E565.MirrorCS", {"start": v(264.23, 155.5) * mm, "end": v(218.16, 116.93) * mm});
            skLineSegment(sketch, "E566.MirrorCS", {"start": v(462.24, 324.27) * mm, "end": v(462.24, 329.91) * mm});
            skLineSegment(sketch, "E567.MirrorCS", {"start": v(483.07, -550.77) * mm, "end": v(420.27, -550.77) * mm});
            skLineSegment(sketch, "E568.MirrorCS", {"start": v(-70.1, 5.43) * mm, "end": v(-83.56, -0.16) * mm});
            skPoint(sketch, "E569.MirrorP", {"position": v(-28.42, -165.52) * mm});
            skLineSegment(sketch, "E570.MirrorCS", {"start": v(-38.58, -10.14) * mm, "end": v(48.16, -134.78) * mm});
            skLineSegment(sketch, "E571.MirrorCS", {"start": v(258.84, 166.58) * mm, "end": v(178.3, 149.6) * mm});
            skPoint(sketch, "E572.MirrorP", {"position": v(99.29, -155.84) * mm});
            skPoint(sketch, "E573.MirrorP", {"position": v(-65.85, -26.54) * mm});
            skPoint(sketch, "E574.MirrorP", {"position": v(162.9, 146.36) * mm});
            skPoint(sketch, "E575.MirrorP", {"position": v(198.34, 86.7) * mm});
            skLineSegment(sketch, "E576.MirrorCS", {"start": v(-62.92, -30.74) * mm, "end": v(14.75, -142.35) * mm});
            skLineSegment(sketch, "E577.MirrorCS", {"start": v(206.2, -119.67) * mm, "end": v(144.4, -140.57) * mm});
            skLineSegment(sketch, "E578.MirrorCS", {"start": v(195.43, 88.52) * mm, "end": v(120.32, 135.57) * mm});
            skPoint(sketch, "E579.MirrorP", {"position": v(50.89, -138.7) * mm});
            skLineSegment(sketch, "E580.MirrorCS", {"start": v(-44.14, -160) * mm, "end": v(-85.13, -150.07) * mm});
            skLineSegment(sketch, "E581.MirrorCS", {"start": v(-53.2, -190.48) * mm, "end": v(-85.13, -182.74) * mm});
            skLineSegment(sketch, "E582.MirrorCS", {"start": v(197.53, -89.08) * mm, "end": v(55.4, -137.16) * mm});
            skPoint(sketch, "E583.MirrorP", {"position": v(462.24, 321.3) * mm});
            skPoint(sketch, "E584.MirrorP", {"position": v(16.87, 115.59) * mm});
            skPoint(sketch, "E585.MirrorP", {"position": v(-40.67, -7.14) * mm});
            skPoint(sketch, "E586.MirrorP", {"position": v(11.49, 146.9) * mm});
            skLineSegment(sketch, "E587.MirrorCS", {"start": v(-25.94, 230.28) * mm, "end": v(9.4, 151.57) * mm});
            skLineSegment(sketch, "E588.MirrorCS", {"start": v(419.51, -509.17) * mm, "end": v(107.33, -221.23) * mm});
            skLineSegment(sketch, "E589.MirrorCS", {"start": v(-13.28, 122.75) * mm, "end": v(-66.8, 8.6) * mm});
            skLineSegment(sketch, "E590.MirrorCS", {"start": v(198.4, 83.27) * mm, "end": v(201.83, -83.54) * mm});
            skPoint(sketch, "E591.MirrorP", {"position": v(-121.6, 363.63) * mm});
            skLineSegment(sketch, "E592.MirrorCS", {"start": v(459.97, 319.4) * mm, "end": v(376.28, 249.33) * mm});
            skLineSegment(sketch, "E593.MirrorCS", {"start": v(493.99, 382.68) * mm, "end": v(493.99, 309.44) * mm});
            skPoint(sketch, "E594.MirrorP", {"position": v(20.06, -182.64) * mm});
            skPoint(sketch, "E595.MirrorP", {"position": v(214.62, 113.96) * mm});
            skLineSegment(sketch, "E596.MirrorCS", {"start": v(-59.58, 230.29) * mm, "end": v(-13.24, 128.07) * mm});
            skPoint(sketch, "E597.MirrorP", {"position": v(283.73, 171.83) * mm});
            skPoint(sketch, "E598.MirrorP", {"position": v(141.92, -141.41) * mm});
            skPoint(sketch, "E599.MirrorP", {"position": v(493.99, 306.48) * mm});
            skPoint(sketch, "E600.MirrorP", {"position": v(230.12, 85.53) * mm});
            skLineSegment(sketch, "E601.MirrorCS", {"start": v(213.75, -122.54) * mm, "end": v(429.34, -501.36) * mm});
            skPoint(sketch, "E602.MirrorP", {"position": v(19.58, -149.29) * mm});
            skLineSegment(sketch, "E603.MirrorCS", {"start": v(333.96, 214.86) * mm, "end": v(16.5, 147.96) * mm});
            skPoint(sketch, "E604.MirrorP", {"position": v(335.51, 215.19) * mm});
            skLineSegment(sketch, "E605.MirrorCS", {"start": v(491.72, 304.57) * mm, "end": v(232.45, 87.48) * mm});
            skPoint(sketch, "E606.MirrorP", {"position": v(76.11, -202.43) * mm});
            skPoint(sketch, "E607.MirrorP", {"position": v(-52.88, -190.56) * mm});
            skLineSegment(sketch, "E608.MirrorCS", {"start": v(75.72, -235.96) * mm, "end": v(-52.57, -190.66) * mm});
            skPoint(sketch, "E609.MirrorP", {"position": v(118.15, 136.93) * mm});
            skPoint(sketch, "E610.MirrorP", {"position": v(-13.6, 125.4) * mm});
            skLineSegment(sketch, "E611.MirrorCS", {"start": v(415.96, -549.1) * mm, "end": v(77.91, -237.28) * mm});
            skLineSegment(sketch, "E612.MirrorCS", {"start": v(234.59, -94.97) * mm, "end": v(488.59, -541.28) * mm});
            skPoint(sketch, "E613.MirrorP", {"position": v(211.15, -117.99) * mm});
            skLineSegment(sketch, "E614.MirrorCS", {"start": v(15.53, 112.72) * mm, "end": v(-39.11, -3.82) * mm});
            skPoint(sketch, "E615.MirrorP", {"position": v(-69.4, 6.37) * mm});
            skPoint(sketch, "E616.MirrorP", {"position": v(-43.83, -160.08) * mm});
            skPoint(sketch, "E617.MirrorP", {"position": v(76.95, -236.4) * mm});
            skPoint(sketch, "E618.MirrorP", {"position": v(103.83, -218) * mm});
            skPoint(sketch, "E619.MirrorP", {"position": v(201.94, -87.59) * mm});
            skLineSegment(sketch, "E620.MirrorCS", {"start": v(230.18, 82.48) * mm, "end": v(233.76, -91.96) * mm});
            skLineSegment(sketch, "E621.MirrorCS", {"start": v(115.64, 136.4) * mm, "end": v(19.97, 116.24) * mm});
            skPoint(sketch, "E622.MirrorP", {"position": v(233.79, -93.57) * mm});
            skLineSegment(sketch, "E623", {"start": v(-686.37, 363.63) * mm, "end": v(-686.37, 348.24) * mm});
            skLineSegment(sketch, "E624", {"start": v(-689.55, 342.74) * mm, "end": v(-702.25, 335.41) * mm});
            skLineSegment(sketch, "E625.trimOffspring", {"start": v(-705.42, 363.63) * mm, "end": v(-705.42, 382.68) * mm});
            skPoint(sketch, "E626.visualSharp", {"position": v(-705.42, 333.58) * mm});
            skArc(sketch, "E626.filletArc", {"start": v(-702.25, 335.41) * mm, "mid": v(-704.57, 333.09) * mm, "end": v(-705.42, 329.91) * mm});
            skPoint(sketch, "E627.visualSharp", {"position": v(-686.37, 344.58) * mm});
            skArc(sketch, "E627.filletArc", {"start": v(-689.55, 342.74) * mm, "mid": v(-687.22, 345.07) * mm, "end": v(-686.37, 348.24) * mm});
            skLineSegment(sketch, "E628.trimOffspring", {"start": v(462.24, 382.68) * mm, "end": v(493.99, 382.68) * mm});
            skLineSegment(sketch, "E629", {"start": v(-181, 230.29) * mm, "end": v(-181, 249.34) * mm});
            skLineSegment(sketch, "E630", {"start": v(-199.64, 249.34) * mm, "end": v(-218.27, 249.34) * mm});
            skLineSegment(sketch, "E631", {"start": v(-218.27, 249.34) * mm, "end": v(-218.27, 230.29) * mm});
            skLineSegment(sketch, "E632", {"start": v(-59.58, 230.29) * mm, "end": v(-59.58, 249.34) * mm});
            skLineSegment(sketch, "E633", {"start": v(-42.76, 249.34) * mm, "end": v(-25.94, 249.34) * mm});
            skLineSegment(sketch, "E634", {"start": v(-25.94, 249.34) * mm, "end": v(-25.94, 230.28) * mm});
            skLineSegment(sketch, "E635", {"start": v(462.24, 363.63) * mm, "end": v(443.19, 363.63) * mm});
            skLineSegment(sketch, "E636", {"start": v(443.19, 363.63) * mm, "end": v(443.19, 348.24) * mm});
            skLineSegment(sketch, "E637", {"start": v(446.36, 342.74) * mm, "end": v(459.06, 335.41) * mm});
            skLineSegment(sketch, "E638.trimOffspring", {"start": v(462.24, 363.63) * mm, "end": v(462.24, 382.68) * mm});
            skPoint(sketch, "E639.visualSharp", {"position": v(443.19, 344.58) * mm});
            skArc(sketch, "E639.filletArc", {"start": v(443.19, 348.24) * mm, "mid": v(444.04, 345.07) * mm, "end": v(446.36, 342.74) * mm});
            skPoint(sketch, "E640.visualSharp", {"position": v(462.24, 333.58) * mm});
            skArc(sketch, "E640.filletArc", {"start": v(462.24, 329.91) * mm, "mid": v(461.39, 333.09) * mm, "end": v(459.06, 335.41) * mm});
            skPoint(sketch, "E641.visualSharp", {"position": v(417.79, -550.77) * mm});
            skArc(sketch, "E641.filletArc", {"start": v(415.96, -549.1) * mm, "mid": v(417.96, -550.34) * mm, "end": v(420.27, -550.77) * mm});
            skPoint(sketch, "E642.visualSharp", {"position": v(493.99, -550.77) * mm});
            skArc(sketch, "E642.filletArc", {"start": v(483.07, -550.77) * mm, "mid": v(488.56, -547.62) * mm, "end": v(488.59, -541.28) * mm});
            skPoint(sketch, "E643.visualSharp", {"position": v(-737.17, -550.77) * mm});
            skArc(sketch, "E643.filletArc", {"start": v(-731.77, -541.28) * mm, "mid": v(-731.74, -547.62) * mm, "end": v(-726.25, -550.77) * mm});
            skPoint(sketch, "E644.visualSharp", {"position": v(-660.97, -550.77) * mm});
            skArc(sketch, "E644.filletArc", {"start": v(-663.45, -550.77) * mm, "mid": v(-661.14, -550.34) * mm, "end": v(-659.15, -549.1) * mm});
            skLineSegment(sketch, "E645", {"start": v(-121.6, -17.37) * mm, "end": v(-121.6, -34.56) * mm, "construction": true});
            skLineSegment(sketch, "E646", {"start": v(-121.6, -150.07) * mm, "end": v(-121.6, -182.74) * mm, "construction": true});
            skLineSegment(sketch, "E647", {"start": v(-70.57, -28.5) * mm, "end": v(-85.13, -34.56) * mm});
            skLineSegment(sketch, "E648", {"start": v(-85.13, -182.74) * mm, "end": v(-85.13, -150.07) * mm, "construction": true});
            skLineSegment(sketch, "E649.trimOffspring", {"start": v(-131.12, -150.07) * mm, "end": v(-131.12, -182.74) * mm, "construction": true});
            skLineSegment(sketch, "E650", {"start": v(-172.61, -28.5) * mm, "end": v(-158.05, -34.56) * mm});
            skPoint(sketch, "E651", {"position": v(-83.56, -17.36) * mm});
            skLineSegment(sketch, "E652", {"start": v(-116.83, -17.36) * mm, "end": v(-124.64, -17.36) * mm});
            skLineSegment(sketch, "E653", {"start": v(-131.12, -182.74) * mm, "end": v(-158.05, -182.74) * mm});
            skLineSegment(sketch, "E654", {"start": v(-131.12, -150.07) * mm, "end": v(-158.05, -150.07) * mm});
            skPoint(sketch, "E655", {"position": v(-85.13, -166.4) * mm});
            skLineSegment(sketch, "E656", {"start": v(-85.13, -166.4) * mm, "end": v(-131.12, -166.4) * mm});
            skLineSegment(sketch, "E657", {"start": v(376.28, 249.33) * mm, "end": v(376.28, 230.28) * mm});
            skLineSegment(sketch, "E658.trimOffspring", {"start": v(353.53, 230.28) * mm, "end": v(336.73, 216.2) * mm});
            skLineSegment(sketch, "E659", {"start": v(376.28, 230.28) * mm, "end": v(353.53, 230.28) * mm});
            skLineSegment(sketch, "E660", {"start": v(-619.47, 249.33) * mm, "end": v(-619.47, 230.28) * mm});
            skLineSegment(sketch, "E661", {"start": v(-619.47, 230.28) * mm, "end": v(-596.72, 230.28) * mm});
            skLineSegment(sketch, "E662.trimOffspring", {"start": v(-596.72, 230.28) * mm, "end": v(-579.91, 216.2) * mm});
            skPoint(sketch, "E663", {"position": v(-42.76, 249.34) * mm});
            skPoint(sketch, "E664", {"position": v(-199.64, 249.34) * mm});
            skLineSegment(sketch, "E665.0", {"start": v(-64.43, 249.34) * mm, "end": v(49.87, 363.64) * mm});
            skLineSegment(sketch, "E666", {"start": v(93.2, 363.64) * mm, "end": v(93.2, 382.69) * mm});
            skLineSegment(sketch, "E667", {"start": v(49.87, 363.64) * mm, "end": v(49.87, 382.69) * mm});
            skLineSegment(sketch, "E668", {"start": v(49.87, 382.69) * mm, "end": v(93.2, 382.69) * mm});
            skLineSegment(sketch, "E669", {"start": v(-64.43, 249.34) * mm, "end": v(-59.58, 249.34) * mm});
            skLineSegment(sketch, "E670", {"start": v(-25.94, 249.34) * mm, "end": v(-21.1, 249.34) * mm});
            skLineSegment(sketch, "E671.trimOffspring", {"start": v(-21.1, 249.34) * mm, "end": v(93.2, 363.64) * mm});
            skLineSegment(sketch, "E672", {"start": v(-42.76, 249.34) * mm, "end": v(-42.76, 230.28) * mm});
            skLineSegment(sketch, "E673.trimOffspring", {"start": v(-59.58, 249.34) * mm, "end": v(-181, 249.34) * mm, "construction": true});
            skLineSegment(sketch, "E674.0", {"start": v(-221.06, 249.34) * mm, "end": v(-335.36, 363.64) * mm});
            skLineSegment(sketch, "E675.0", {"start": v(-176.16, 249.34) * mm, "end": v(-290.46, 363.64) * mm});
            skLineSegment(sketch, "E676", {"start": v(-176.16, 249.34) * mm, "end": v(-181, 249.34) * mm});
            skLineSegment(sketch, "E677", {"start": v(-218.27, 249.34) * mm, "end": v(-221.06, 249.34) * mm});
            skLineSegment(sketch, "E678", {"start": v(-335.36, 363.64) * mm, "end": v(-335.36, 382.69) * mm});
            skLineSegment(sketch, "E679", {"start": v(-290.46, 363.64) * mm, "end": v(-290.46, 382.69) * mm});
            skLineSegment(sketch, "E680", {"start": v(-290.46, 382.69) * mm, "end": v(-335.36, 382.69) * mm});
            skLineSegment(sketch, "E681", {"start": v(-158.05, -150.07) * mm, "end": v(-158.05, -182.74) * mm, "construction": true});
            skLineSegment(sketch, "E682", {"start": v(-199.64, 249.34) * mm, "end": v(-199.64, 230.29) * mm});
            skPoint(sketch, "E683.orphan", {"position": v(-83.56, -34.55) * mm});
            skLineSegment(sketch, "E684", {"start": v(-85.13, -182.74) * mm, "end": v(-131.12, -182.74) * mm, "construction": true});
            skLineSegment(sketch, "E685", {"start": v(-85.13, -34.56) * mm, "end": v(-158.05, -34.56) * mm});
            skLineSegment(sketch, "E686", {"start": v(-85.13, -150.07) * mm, "end": v(-131.12, -150.07) * mm});
            skLineSegment(sketch, "E687", {"start": v(-85.13, -182.74) * mm, "end": v(-131.12, -182.74) * mm});
            skLineSegment(sketch, "E688", {"start": v(-157.02, -0.16) * mm, "end": v(-143.69, -0.16) * mm});
            skLineSegment(sketch, "E689", {"start": v(-83.56, -0.16) * mm, "end": v(-90.44, -0.16) * mm});
            skPoint(sketch, "E690", {"position": v(-151.32, -17.37) * mm});
            skLineSegment(sketch, "E691", {"start": v(-83.56, -0.16) * mm, "end": v(-96.9, -0.16) * mm});
            skLineSegment(sketch, "E692", {"start": v(-96.9, -0.16) * mm, "end": v(-115.95, 0) * mm});
            skLineSegment(sketch, "E693", {"start": v(-143.69, -0.16) * mm, "end": v(-126.36, -0.01) * mm});
            skPoint(sketch, "E694", {"position": v(-121.6, -34.56) * mm});
            skLineSegment(sketch, "E695", {"start": v(-126.36, -24.23) * mm, "end": v(-116.83, -24.23) * mm});
            skPoint(sketch, "E696", {"position": v(-120.88, -24.93) * mm});
            skLineSegment(sketch, "E697", {"start": v(-121.6, -24.23) * mm, "end": v(-121.6, -23.58) * mm});
            skLineSegment(sketch, "E698", {"start": v(-116.83, -24.23) * mm, "end": v(-116.83, -17.36) * mm});
            skPoint(sketch, "E699.orphan", {"position": v(-116.83, -23.64) * mm});
            skLineSegment(sketch, "E700", {"start": v(-116.83, -17.36) * mm, "end": v(-116.83, 0) * mm});
            skLineSegment(sketch, "E701", {"start": v(-116.83, 0) * mm, "end": v(-115.95, 0) * mm});
            skLineSegment(sketch, "E702", {"start": v(-126.36, -24.23) * mm, "end": v(-126.36, 0) * mm});
            skLineSegment(sketch, "E703", {"start": v(-124.64, -17.36) * mm, "end": v(-126.36, -17.36) * mm});
            skPoint(sketch, "E704.start.orphan", {"position": v(-124.64, 0) * mm});
            skSolve(sketch);
        }
        {
            var Q0;
            Q0=makeQuery(id+"F4.imprint","IMPRINT",FACE,{"disambiguationData":[TD([[makeQuery(id+"F4.imprint","IMPRINT",EDGE,{"derivedFrom":sQuery(id+"F4.wireOp",EDGE,"E214.top")}),-1.0]])]});
            extrude(context, id + "F6", {"entities" : qUnion([Q0]), "endBound" : BoundingType.SYMMETRIC, "depth" : 19.05 * mm});
        }
        {
            var Q0;
            Q0=makeQuery(id+"F5.imprint","IMPRINT",FACE,{"disambiguationData":[TD([[makeQuery(id+"F5.imprint","IMPRINT",EDGE,{"derivedFrom":sQuery(id+"F5.wireOp",EDGE,"E458.top")}),-1.0]])]});
            extrude(context, id + "F7", {"entities" : qUnion([Q0]), "endBound" : BoundingType.SYMMETRIC, "depth" : 19.05 * mm});
        }
        {
            var Q0;
            Q0=qCreatedBy(id+"F1.planeOp",FACE);
            var sketch = newSketch(context, id + "F8", { "sketchPlane" : qUnion([Q0])});
            skLineSegment(sketch, "E705.0", {"start": v(-640.74, 15.45) * mm, "end": v(234.28, 377.87) * mm});
            skLineSegment(sketch, "E706.0", {"start": v(403.6, 9.57) * mm, "end": v(256.36, 364.65) * mm});
            skLineSegment(sketch, "E707.0", {"start": v(-476.6, -376.67) * mm, "end": v(397.36, -15.42) * mm});
            skLineSegment(sketch, "E708.0", {"start": v(-646.9, -9.54) * mm, "end": v(-498.75, -363.46) * mm});
            skPoint(sketch, "E709", {"position": v(256.36, 364.65) * mm});
            skPoint(sketch, "E710", {"position": v(403.6, 9.57) * mm});
            skPoint(sketch, "E711", {"position": v(-498.75, -363.46) * mm});
            skPoint(sketch, "E712", {"position": v(-646.9, -9.54) * mm});
            skLineSegment(sketch, "E713", {"start": v(223.5, 358.78) * mm, "end": v(236.98, 345.25) * mm});
            skLineSegment(sketch, "E714", {"start": v(236.98, 345.25) * mm, "end": v(256.36, 364.65) * mm});
            skLineSegment(sketch, "E715", {"start": v(223.5, 358.78) * mm, "end": v(241.57, 376.86) * mm});
            skLineSegment(sketch, "E716", {"start": v(376.22, 9.54) * mm, "end": v(376.22, -9.56) * mm});
            skLineSegment(sketch, "E717", {"start": v(376.22, -9.56) * mm, "end": v(401.81, -9.57) * mm});
            skLineSegment(sketch, "E718", {"start": v(376.22, 9.54) * mm, "end": v(403.6, 9.57) * mm});
            skLineSegment(sketch, "E719", {"start": v(-619.44, 9.53) * mm, "end": v(-645.19, 9.57) * mm});
            skLineSegment(sketch, "E720", {"start": v(-646.9, -9.54) * mm, "end": v(-619.44, -9.54) * mm});
            skLineSegment(sketch, "E721", {"start": v(-619.44, -9.54) * mm, "end": v(-619.44, 9.53) * mm});
            skLineSegment(sketch, "E722", {"start": v(-498.75, -363.46) * mm, "end": v(-480.6, -345.3) * mm});
            skLineSegment(sketch, "E723", {"start": v(-480.6, -345.3) * mm, "end": v(-467.1, -358.79) * mm});
            skLineSegment(sketch, "E724", {"start": v(-467.1, -358.79) * mm, "end": v(-483.91, -375.65) * mm});
            skLineSegment(sketch, "E725", {"start": v(-182.7, -74.37) * mm, "end": v(-157.72, -49.46) * mm});
            skLineSegment(sketch, "E726", {"start": v(-157.72, -49.46) * mm, "end": v(-171.3, -35.85) * mm});
            skLineSegment(sketch, "E727", {"start": v(-171.3, -35.85) * mm, "end": v(-196.28, -60.76) * mm});
            skLineSegment(sketch, "E728", {"start": v(-182.7, -74.37) * mm, "end": v(-196.28, -60.76) * mm});
            skLineSegment(sketch, "E729", {"start": v(-218.3, -9.52) * mm, "end": v(-181.02, -9.52) * mm});
            skLineSegment(sketch, "E730", {"start": v(-181.02, -9.52) * mm, "end": v(-181.02, 9.55) * mm});
            skLineSegment(sketch, "E731", {"start": v(-181.02, 9.55) * mm, "end": v(-218.3, 9.55) * mm});
            skLineSegment(sketch, "E732", {"start": v(-218.3, -9.52) * mm, "end": v(-218.3, 9.55) * mm});
            skLineSegment(sketch, "E733", {"start": v(-72.33, 36.01) * mm, "end": v(-47.43, 60.9) * mm});
            skLineSegment(sketch, "E734", {"start": v(-47.43, 60.9) * mm, "end": v(-60.9, 74.38) * mm});
            skLineSegment(sketch, "E735", {"start": v(-60.9, 74.38) * mm, "end": v(-85.8, 49.48) * mm});
            skLineSegment(sketch, "E736", {"start": v(-72.33, 36.01) * mm, "end": v(-85.8, 49.48) * mm});
            skLineSegment(sketch, "E737", {"start": v(-59.6, -9.5) * mm, "end": v(-25.92, -9.5) * mm});
            skLineSegment(sketch, "E738", {"start": v(-25.92, -9.5) * mm, "end": v(-25.92, 9.56) * mm});
            skLineSegment(sketch, "E739", {"start": v(-25.92, 9.56) * mm, "end": v(-59.6, 9.56) * mm});
            skLineSegment(sketch, "E740", {"start": v(-59.6, -9.5) * mm, "end": v(-59.6, 9.56) * mm});
            skLineSegment(sketch, "E741", {"start": v(-481.46, -376.66) * mm, "end": v(-483.91, -375.65) * mm});
            skArc(sketch, "E742.filletArc", {"start": v(-481.46, -376.66) * mm, "mid": v(-479.03, -377.15) * mm, "end": v(-476.6, -376.67) * mm});
            skLineSegment(sketch, "E743", {"start": v(400.8, -12) * mm, "end": v(401.81, -9.57) * mm});
            skLineSegment(sketch, "E744", {"start": v(-644.17, 12.01) * mm, "end": v(-645.19, 9.57) * mm});
            skLineSegment(sketch, "E745", {"start": v(239.14, 377.87) * mm, "end": v(241.57, 376.86) * mm});
            skPoint(sketch, "E746.visualSharp", {"position": v(236.71, 378.88) * mm});
            skArc(sketch, "E746.filletArc", {"start": v(239.14, 377.87) * mm, "mid": v(236.71, 378.35) * mm, "end": v(234.28, 377.87) * mm});
            skPoint(sketch, "E747.visualSharp", {"position": v(-643.17, 14.44) * mm});
            skArc(sketch, "E747.filletArc", {"start": v(-640.74, 15.45) * mm, "mid": v(-642.8, 14.07) * mm, "end": v(-644.17, 12.01) * mm});
            skPoint(sketch, "E748.visualSharp", {"position": v(399.8, -14.42) * mm});
            skArc(sketch, "E748.filletArc", {"start": v(397.36, -15.42) * mm, "mid": v(399.43, -14.05) * mm, "end": v(400.8, -12) * mm});
            skSolve(sketch);
        }
        {
            var Q0;
            Q0=makeQuery(id+"F8.imprint","IMPRINT",FACE,{"disambiguationData":[TD([[makeQuery(id+"F8.imprint","IMPRINT",EDGE,{"derivedFrom":sQuery(id+"F8.wireOp",EDGE,"E705.0")}),-1.0]])]});
            extrude(context, id + "F9", {"entities" : qUnion([Q0]), "depth" : 19.05 * mm});
        }
        {
            var Q0;
            Q0=makeQuery(id+"F5.imprint","IMPRINT",FACE,{"disambiguationData":[TD([[makeQuery(id+"F5.imprint","IMPRINT",EDGE,{"derivedFrom":sQuery(id+"F5.wireOp",EDGE,"E491")}),1.0]])]});
            var Q1;
            Q1=makeQuery(id+"F5.imprint","IMPRINT",FACE,{"disambiguationData":[TD([[makeQuery(id+"F5.imprint","IMPRINT",EDGE,{"derivedFrom":sQuery(id+"F5.wireOp",EDGE,"E564.MirrorCS")}),-1.0]])]});
            extrude(context, id + "F10", {"entities" : qUnion([Q0, Q1]), "endBound" : BoundingType.SYMMETRIC, "depth" : 19.05 * mm});
        }
        {
            var Q0;
            Q0=makeQuery(id+"F4.imprint","IMPRINT",FACE,{"disambiguationData":[TD([[makeQuery(id+"F4.imprint","IMPRINT",EDGE,{"derivedFrom":sQuery(id+"F4.wireOp",EDGE,"E320.MirrorCS")}),-1.0]])]});
            var Q1;
            Q1=makeQuery(id+"F4.imprint","IMPRINT",FACE,{"disambiguationData":[TD([[makeQuery(id+"F4.imprint","IMPRINT",EDGE,{"derivedFrom":sQuery(id+"F4.wireOp",EDGE,"E247")}),1.0]])]});
            extrude(context, id + "F11", {"entities" : qUnion([Q0, Q1]), "endBound" : BoundingType.SYMMETRIC, "depth" : 19.05 * mm});
        }
        {
            var Q0;
            Q0=qCreatedBy(id+"F2.planeOp",FACE);
            var sketch = newSketch(context, id + "F12", { "sketchPlane" : qUnion([Q0])});
            skLineSegment(sketch, "E749", {"start": v(494.04, -9.5) * mm, "end": v(462.24, -9.5) * mm});
            skLineSegment(sketch, "E750", {"start": v(462.24, -9.5) * mm, "end": v(462.24, 9.57) * mm});
            skLineSegment(sketch, "E751", {"start": v(462.24, 9.57) * mm, "end": v(493.99, 9.53) * mm});
            skLineSegment(sketch, "E752", {"start": v(306.76, 442.05) * mm, "end": v(284.27, 419.52) * mm});
            skLineSegment(sketch, "E753", {"start": v(284.27, 419.52) * mm, "end": v(297.77, 406.05) * mm});
            skLineSegment(sketch, "E754", {"start": v(297.77, 406.05) * mm, "end": v(320.23, 428.54) * mm});
            skLineSegment(sketch, "E755", {"start": v(-737.16, 9.56) * mm, "end": v(-705.4, 9.56) * mm});
            skLineSegment(sketch, "E756", {"start": v(-705.4, 9.56) * mm, "end": v(-705.4, -9.52) * mm});
            skLineSegment(sketch, "E757", {"start": v(-705.4, -9.52) * mm, "end": v(-737.2, -9.51) * mm});
            skLineSegment(sketch, "E758", {"start": v(-550.34, -442.02) * mm, "end": v(-527.9, -419.56) * mm});
            skLineSegment(sketch, "E759", {"start": v(-527.9, -419.56) * mm, "end": v(-541.35, -406.1) * mm});
            skLineSegment(sketch, "E760", {"start": v(-541.35, -406.1) * mm, "end": v(-563.78, -428.55) * mm});
            skPoint(sketch, "E761", {"position": v(-28.15, -225.76) * mm});
            skLineSegment(sketch, "E762", {"start": v(-57.32, -155.37) * mm, "end": v(-215.23, 225.8) * mm, "construction": true});
            skPoint(sketch, "E763", {"position": v(-650.5, -219.03) * mm});
            skLineSegment(sketch, "E764", {"start": v(-57.32, -155.37) * mm, "end": v(153.88, -67.87) * mm});
            skLineSegment(sketch, "E765", {"start": v(153.88, -67.87) * mm, "end": v(-57.32, -155.37) * mm});
            skLineSegment(sketch, "E766", {"start": v(-57.32, -155.37) * mm, "end": v(-268.5, -242.86) * mm});
            skLineSegment(sketch, "E767", {"start": v(153.88, -67.87) * mm, "end": v(316.77, -89.3) * mm});
            skLineSegment(sketch, "E768", {"start": v(-650.5, -219.03) * mm, "end": v(407.25, 218.7) * mm, "construction": true});
            skLineSegment(sketch, "E769", {"start": v(-268.5, -242.86) * mm, "end": v(-368.37, -373.02) * mm});
            skLineSegment(sketch, "E770", {"start": v(129.5, 113.01) * mm, "end": v(129.5, 100.25) * mm});
            skLineSegment(sketch, "E771", {"start": v(255.5, 142.67) * mm, "end": v(266.51, 170.86) * mm});
            skLineSegment(sketch, "E772", {"start": v(266.51, 170.86) * mm, "end": v(129.5, 113.01) * mm});
            skLineSegment(sketch, "E773", {"start": v(191.26, 194.48) * mm, "end": v(263.24, 177.4) * mm});
            skLineSegment(sketch, "E774", {"start": v(191.26, 194.48) * mm, "end": v(170.98, 184.84) * mm});
            skLineSegment(sketch, "E775", {"start": v(170.98, 184.84) * mm, "end": v(152.05, 164.14) * mm});
            skLineSegment(sketch, "E776", {"start": v(152.05, 164.14) * mm, "end": v(129.8, 122.2) * mm});
            skLineSegment(sketch, "E777", {"start": v(254.12, 135.67) * mm, "end": v(217.08, 94.02) * mm});
            skLineSegment(sketch, "E778", {"start": v(217.08, 94.02) * mm, "end": v(132.75, 93.96) * mm});
            skLineSegment(sketch, "E779", {"start": v(183.9, 308.48) * mm, "end": v(167.52, 296.1) * mm});
            skLineSegment(sketch, "E780", {"start": v(167.52, 296.1) * mm, "end": v(184.57, 285.27) * mm});
            skLineSegment(sketch, "E781", {"start": v(184.57, 285.27) * mm, "end": v(183.9, 308.48) * mm});
            skLineSegment(sketch, "E782", {"start": v(162, 290.68) * mm, "end": v(182.88, 277.32) * mm});
            skPoint(sketch, "E782.startSnap0", {"position": v(176.04, 290.68) * mm});
            skLineSegment(sketch, "E783", {"start": v(182.88, 277.32) * mm, "end": v(194.08, 251.87) * mm});
            skLineSegment(sketch, "E784", {"start": v(194.08, 251.87) * mm, "end": v(164.58, 243.15) * mm});
            skLineSegment(sketch, "E785", {"start": v(164.58, 243.15) * mm, "end": v(146.47, 245.9) * mm});
            skLineSegment(sketch, "E786", {"start": v(146.47, 245.9) * mm, "end": v(143.5, 269.25) * mm});
            skLineSegment(sketch, "E787", {"start": v(143.5, 269.25) * mm, "end": v(162, 290.68) * mm});
            skLineSegment(sketch, "E788", {"start": v(191.36, 310.52) * mm, "end": v(191.36, 281.37) * mm});
            skLineSegment(sketch, "E789", {"start": v(191.36, 281.37) * mm, "end": v(202.65, 253.2) * mm});
            skLineSegment(sketch, "E790", {"start": v(202.65, 253.2) * mm, "end": v(213.6, 257.59) * mm});
            skLineSegment(sketch, "E791", {"start": v(213.6, 257.59) * mm, "end": v(191.36, 310.52) * mm});
            skLineSegment(sketch, "E792.MirrorCS", {"start": v(-530.06, -50.35) * mm, "end": v(-540.9, -55) * mm});
            skLineSegment(sketch, "E793.MirrorCS", {"start": v(-535.55, 4.81) * mm, "end": v(-539.95, -14.89) * mm});
            skLineSegment(sketch, "E794.MirrorCS", {"start": v(-555.9, 2) * mm, "end": v(-535.55, 4.81) * mm});
            skLineSegment(sketch, "E795.MirrorCS", {"start": v(-496.04, -30.53) * mm, "end": v(-485.18, -15.78) * mm});
            skLineSegment(sketch, "E796.MirrorCS", {"start": v(-527.83, 4.9) * mm, "end": v(-533.14, -19.32) * mm});
            skLineSegment(sketch, "E797.MirrorCS", {"start": v(-539.95, -14.89) * mm, "end": v(-555.9, 2) * mm});
            skPoint(sketch, "E798.MirrorP", {"position": v(-537.75, -5.04) * mm});
            skLineSegment(sketch, "E799.MirrorCS", {"start": v(-499.59, 2.83) * mm, "end": v(-527.83, 4.9) * mm});
            skLineSegment(sketch, "E800.MirrorCS", {"start": v(-542, -22.45) * mm, "end": v(-530.06, -50.35) * mm});
            skLineSegment(sketch, "E801.MirrorCS", {"start": v(-533.14, -19.32) * mm, "end": v(-523.06, -45.23) * mm});
            skLineSegment(sketch, "E802.MirrorCS", {"start": v(-562.6, -1.85) * mm, "end": v(-542, -22.45) * mm});
            skLineSegment(sketch, "E803.MirrorCS", {"start": v(-485.18, -15.78) * mm, "end": v(-499.59, 2.83) * mm});
            skLineSegment(sketch, "E804.MirrorCS", {"start": v(-523.06, -45.23) * mm, "end": v(-496.04, -30.53) * mm});
            skLineSegment(sketch, "E805.MirrorCS", {"start": v(-540.9, -55) * mm, "end": v(-562.6, -1.85) * mm});
            skLineSegment(sketch, "E806", {"start": v(494.04, -9.5) * mm, "end": v(494.03, -11.68) * mm});
            skLineSegment(sketch, "E807", {"start": v(493.99, 9.53) * mm, "end": v(494, 14.61) * mm});
            skLineSegment(sketch, "E808", {"start": v(306.76, 442.05) * mm, "end": v(305.27, 443.54) * mm});
            skLineSegment(sketch, "E809", {"start": v(320.23, 428.54) * mm, "end": v(323.83, 424.95) * mm});
            skLineSegment(sketch, "E810", {"start": v(-737.16, 9.56) * mm, "end": v(-737.17, 11.65) * mm});
            skLineSegment(sketch, "E811", {"start": v(-737.2, -9.51) * mm, "end": v(-737.2, -14.6) * mm});
            skLineSegment(sketch, "E812", {"start": v(-563.78, -428.55) * mm, "end": v(-567.38, -424.96) * mm});
            skLineSegment(sketch, "E813", {"start": v(-550.34, -442.02) * mm, "end": v(-548.82, -443.53) * mm});
            skLineSegment(sketch, "E814", {"start": v(-568.76, -422.9) * mm, "end": v(-736.72, -17.03) * mm});
            skLineSegment(sketch, "E815", {"start": v(-733.25, 17.54) * mm, "end": v(298.35, 444.91) * mm});
            skLineSegment(sketch, "E816", {"start": v(325.21, 422.89) * mm, "end": v(493.5, 17.05) * mm});
            skLineSegment(sketch, "E817", {"start": v(-541.92, -444.89) * mm, "end": v(-368.37, -373.02) * mm});
            skLineSegment(sketch, "E818.trimOffspring", {"start": v(316.77, -89.3) * mm, "end": v(490.11, -17.53) * mm});
            skPoint(sketch, "E819.visualSharp", {"position": v(494.02, -15.91) * mm});
            skArc(sketch, "E819.filletArc", {"start": v(490.11, -17.53) * mm, "mid": v(492.96, -15.2) * mm, "end": v(494.03, -11.68) * mm});
            skPoint(sketch, "E820.visualSharp", {"position": v(494, 15.88) * mm});
            skArc(sketch, "E820.filletArc", {"start": v(494, 14.61) * mm, "mid": v(493.87, 15.85) * mm, "end": v(493.5, 17.05) * mm});
            skPoint(sketch, "E821.visualSharp", {"position": v(-545.82, -446.5) * mm});
            skArc(sketch, "E821.filletArc", {"start": v(-548.82, -443.53) * mm, "mid": v(-545.58, -445.25) * mm, "end": v(-541.92, -444.89) * mm});
            skPoint(sketch, "E822.visualSharp", {"position": v(-568.28, -424.06) * mm});
            skArc(sketch, "E822.filletArc", {"start": v(-568.76, -422.9) * mm, "mid": v(-568.17, -424) * mm, "end": v(-567.38, -424.96) * mm});
            skPoint(sketch, "E823.visualSharp", {"position": v(324.73, 424.06) * mm});
            skArc(sketch, "E823.filletArc", {"start": v(325.21, 422.89) * mm, "mid": v(324.62, 423.99) * mm, "end": v(323.83, 424.95) * mm});
            skPoint(sketch, "E824.visualSharp", {"position": v(302.27, 446.54) * mm});
            skArc(sketch, "E824.filletArc", {"start": v(305.27, 443.54) * mm, "mid": v(302.02, 445.27) * mm, "end": v(298.35, 444.91) * mm});
            skPoint(sketch, "E825.visualSharp", {"position": v(-737.18, 15.91) * mm});
            skArc(sketch, "E825.filletArc", {"start": v(-733.25, 17.54) * mm, "mid": v(-736.1, 15.2) * mm, "end": v(-737.17, 11.65) * mm});
            skPoint(sketch, "E826.visualSharp", {"position": v(-737.2, -15.86) * mm});
            skArc(sketch, "E826.filletArc", {"start": v(-737.2, -14.6) * mm, "mid": v(-737.08, -15.84) * mm, "end": v(-736.72, -17.03) * mm});
            skLineSegment(sketch, "E827", {"start": v(-8.42, 126.87) * mm, "end": v(5.07, 113.38) * mm});
            skLineSegment(sketch, "E828", {"start": v(5.07, 113.38) * mm, "end": v(36.87, 145.13) * mm});
            skLineSegment(sketch, "E829", {"start": v(36.87, 145.13) * mm, "end": v(23.36, 158.67) * mm});
            skLineSegment(sketch, "E830", {"start": v(23.36, 158.67) * mm, "end": v(-8.42, 126.87) * mm});
            skLineSegment(sketch, "E831", {"start": v(49.83, 9.57) * mm, "end": v(49.83, -9.56) * mm});
            skLineSegment(sketch, "E832", {"start": v(49.83, -9.56) * mm, "end": v(93.24, -9.55) * mm});
            skLineSegment(sketch, "E833", {"start": v(93.24, -9.55) * mm, "end": v(93.23, 9.55) * mm});
            skLineSegment(sketch, "E834", {"start": v(93.23, 9.55) * mm, "end": v(49.83, 9.57) * mm});
            skLineSegment(sketch, "E835", {"start": v(-335.42, 9.57) * mm, "end": v(-335.42, -9.56) * mm});
            skLineSegment(sketch, "E836", {"start": v(-335.42, -9.56) * mm, "end": v(-290.42, -9.56) * mm});
            skLineSegment(sketch, "E837", {"start": v(-290.42, -9.56) * mm, "end": v(-290.41, 9.56) * mm});
            skLineSegment(sketch, "E838", {"start": v(-290.41, 9.56) * mm, "end": v(-335.42, 9.57) * mm});
            skLineSegment(sketch, "E839", {"start": v(-280.49, -145.15) * mm, "end": v(-266.95, -158.64) * mm});
            skLineSegment(sketch, "E840", {"start": v(-266.95, -158.64) * mm, "end": v(-235.16, -126.86) * mm});
            skLineSegment(sketch, "E841", {"start": v(-235.16, -126.86) * mm, "end": v(-248.67, -113.36) * mm});
            skLineSegment(sketch, "E842", {"start": v(-248.67, -113.36) * mm, "end": v(-280.49, -145.15) * mm});
            skSolve(sketch);
        }
        {
            var Q0;
            Q0=makeQuery(id+"F12.imprint","IMPRINT",FACE,{"disambiguationData":[TD([[makeQuery(id+"F12.imprint","IMPRINT",EDGE,{"derivedFrom":sQuery(id+"F12.wireOp",EDGE,"E749")}),1.0]])]});
            extrude(context, id + "F13", {"entities" : qUnion([Q0]), "depth" : 19.05 * mm});
        }
    });
